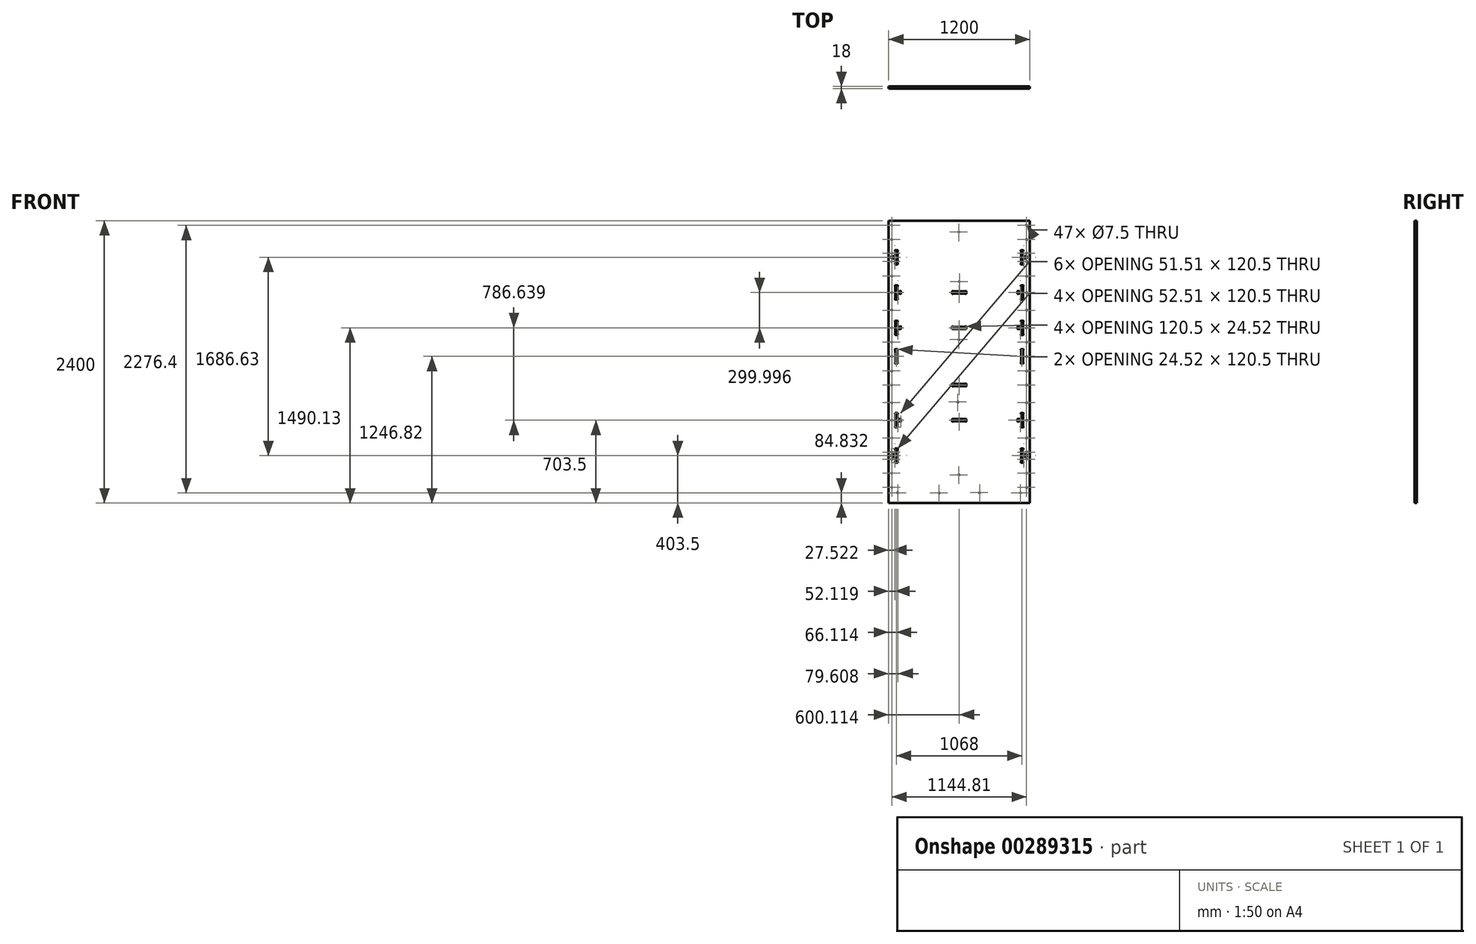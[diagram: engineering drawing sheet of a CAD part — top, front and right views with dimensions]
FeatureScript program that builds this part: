
annotation { "Feature Type Name" : "Feature", "Feature Type Description" : "" }
export const myFeature = defineFeature(function(context is Context, id is Id, definition is map)
    precondition{}
    {
        {
            var Q0;
            Q0=qCreatedBy(makeId("Front.planeOp"),FACE);
            var sketch = newSketch(context, id + "F0", { "sketchPlane" : qUnion([Q0])});
            skLineSegment(sketch, "E0", {"start": v(-600, -1200) * mm, "end": v(600, -1200) * mm});
            skLineSegment(sketch, "E1", {"start": v(600, -1200) * mm, "end": v(600, 1200) * mm});
            skLineSegment(sketch, "E2", {"start": v(600, 1200) * mm, "end": v(-600, 1200) * mm});
            skLineSegment(sketch, "E3", {"start": v(-600, 1200) * mm, "end": v(-600, -1200) * mm});
            skLineSegment(sketch, "E4", {"start": v(-599.64, -1096.25) * mm, "end": v(-543.14, -1096.25) * mm});
            skLineSegment(sketch, "E5", {"start": v(-543.14, -1096.25) * mm, "end": v(-543.14, -1042.52) * mm});
            skLineSegment(sketch, "E6", {"start": v(-543.14, -1042.52) * mm, "end": v(-543.14, -1042.29) * mm});
            skLineSegment(sketch, "E7", {"start": v(-543.14, -1042.29) * mm, "end": v(-543.37, -1042.27) * mm});
            skArc(sketch, "E8", {"start": v(-543.37, -1042.27) * mm, "mid": v(-546.15, -1039.15) * mm, "end": v(-543.14, -1036.25) * mm});
            skLineSegment(sketch, "E9", {"start": v(-543.14, -1036.25) * mm, "end": v(-524.64, -1036.25) * mm});
            skArc(sketch, "E10", {"start": v(-524.64, -1036.25) * mm, "mid": v(-521.63, -1039.15) * mm, "end": v(-524.4, -1042.27) * mm});
            skLineSegment(sketch, "E11", {"start": v(-524.4, -1042.27) * mm, "end": v(-524.64, -1042.29) * mm});
            skLineSegment(sketch, "E12", {"start": v(-524.64, -1042.29) * mm, "end": v(-524.64, -1042.52) * mm});
            skLineSegment(sketch, "E13", {"start": v(-524.64, -1042.52) * mm, "end": v(-524.64, -1087.24) * mm});
            skLineSegment(sketch, "E14", {"start": v(-524.64, -1087.24) * mm, "end": v(-500.9, -1087.24) * mm});
            skLineSegment(sketch, "E15", {"start": v(-500.9, -1087.24) * mm, "end": v(-500.67, -1087.24) * mm});
            skLineSegment(sketch, "E16", {"start": v(-500.67, -1087.24) * mm, "end": v(-500.66, -1087) * mm});
            skArc(sketch, "E17", {"start": v(-500.66, -1087) * mm, "mid": v(-497.54, -1084.22) * mm, "end": v(-494.64, -1087.24) * mm});
            skLineSegment(sketch, "E18", {"start": v(-494.64, -1087.24) * mm, "end": v(-494.64, -1096.25) * mm});
            skLineSegment(sketch, "E19", {"start": v(-494.64, -1096.25) * mm, "end": v(-60.14, -1096.25) * mm});
            skLineSegment(sketch, "E20", {"start": v(-60.14, -1096.25) * mm, "end": v(-60.14, -1087.25) * mm});
            skArc(sketch, "E21", {"start": v(-60.14, -1087.25) * mm, "mid": v(-57.24, -1084.24) * mm, "end": v(-54.11, -1087.02) * mm});
            skLineSegment(sketch, "E22", {"start": v(-54.11, -1087.02) * mm, "end": v(-54.1, -1087.25) * mm});
            skLineSegment(sketch, "E23", {"start": v(-54.1, -1087.25) * mm, "end": v(-53.87, -1087.25) * mm});
            skLineSegment(sketch, "E24", {"start": v(-53.87, -1087.25) * mm, "end": v(54.1, -1087.25) * mm});
            skLineSegment(sketch, "E25", {"start": v(54.1, -1087.25) * mm, "end": v(54.33, -1087.25) * mm});
            skLineSegment(sketch, "E26", {"start": v(54.33, -1087.25) * mm, "end": v(54.34, -1087.02) * mm});
            skArc(sketch, "E27", {"start": v(54.34, -1087.02) * mm, "mid": v(57.47, -1084.23) * mm, "end": v(60.36, -1087.25) * mm});
            skLineSegment(sketch, "E28", {"start": v(60.36, -1087.25) * mm, "end": v(60.36, -1096.26) * mm});
            skLineSegment(sketch, "E29", {"start": v(60.36, -1096.26) * mm, "end": v(494.86, -1096.23) * mm});
            skLineSegment(sketch, "E30", {"start": v(494.86, -1096.23) * mm, "end": v(494.86, -1087.26) * mm});
            skArc(sketch, "E31", {"start": v(494.86, -1087.26) * mm, "mid": v(497.76, -1084.25) * mm, "end": v(500.89, -1087.03) * mm});
            skLineSegment(sketch, "E32", {"start": v(500.89, -1087.03) * mm, "end": v(500.9, -1087.26) * mm});
            skLineSegment(sketch, "E33", {"start": v(500.9, -1087.26) * mm, "end": v(501.13, -1087.26) * mm});
            skLineSegment(sketch, "E34", {"start": v(501.13, -1087.26) * mm, "end": v(524.86, -1087.26) * mm});
            skLineSegment(sketch, "E35", {"start": v(524.86, -1087.26) * mm, "end": v(524.86, -1042.54) * mm});
            skLineSegment(sketch, "E36", {"start": v(524.86, -1042.54) * mm, "end": v(524.86, -1042.3) * mm});
            skLineSegment(sketch, "E37", {"start": v(524.86, -1042.3) * mm, "end": v(524.63, -1042.29) * mm});
            skArc(sketch, "E38", {"start": v(524.63, -1042.29) * mm, "mid": v(521.85, -1039.16) * mm, "end": v(524.86, -1036.27) * mm});
            skLineSegment(sketch, "E39", {"start": v(524.86, -1036.27) * mm, "end": v(543.36, -1036.27) * mm});
            skArc(sketch, "E40", {"start": v(543.36, -1036.27) * mm, "mid": v(546.37, -1039.17) * mm, "end": v(543.6, -1042.29) * mm});
            skLineSegment(sketch, "E41", {"start": v(543.6, -1042.29) * mm, "end": v(543.36, -1042.3) * mm});
            skLineSegment(sketch, "E42", {"start": v(543.36, -1042.3) * mm, "end": v(543.36, -1042.54) * mm});
            skLineSegment(sketch, "E43", {"start": v(543.36, -1042.54) * mm, "end": v(543.36, -1096.26) * mm});
            skLineSegment(sketch, "E44", {"start": v(543.36, -1096.26) * mm, "end": v(599.86, -1096.26) * mm});
            skLineSegment(sketch, "E45", {"start": v(599.86, -1096.26) * mm, "end": v(599.86, 1189.86) * mm});
            skLineSegment(sketch, "E46", {"start": v(599.86, 1189.86) * mm, "end": v(543.36, 1189.86) * mm});
            skLineSegment(sketch, "E47", {"start": v(543.36, 1189.86) * mm, "end": v(543.36, 1136.14) * mm});
            skLineSegment(sketch, "E48", {"start": v(543.36, 1136.14) * mm, "end": v(543.36, 1135.91) * mm});
            skLineSegment(sketch, "E49", {"start": v(543.36, 1135.91) * mm, "end": v(543.6, 1135.9) * mm});
            skArc(sketch, "E50", {"start": v(543.6, 1135.9) * mm, "mid": v(546.38, 1132.77) * mm, "end": v(543.36, 1129.87) * mm});
            skLineSegment(sketch, "E51", {"start": v(543.36, 1129.87) * mm, "end": v(524.86, 1129.87) * mm});
            skArc(sketch, "E52", {"start": v(524.86, 1129.87) * mm, "mid": v(521.85, 1132.77) * mm, "end": v(524.63, 1135.9) * mm});
            skLineSegment(sketch, "E53", {"start": v(524.63, 1135.9) * mm, "end": v(524.86, 1135.91) * mm});
            skLineSegment(sketch, "E54", {"start": v(524.86, 1135.91) * mm, "end": v(524.86, 1136.14) * mm});
            skLineSegment(sketch, "E55", {"start": v(524.86, 1136.14) * mm, "end": v(524.86, 1180.87) * mm});
            skLineSegment(sketch, "E56", {"start": v(524.86, 1180.87) * mm, "end": v(501.13, 1180.87) * mm});
            skLineSegment(sketch, "E57", {"start": v(501.13, 1180.87) * mm, "end": v(500.9, 1180.87) * mm});
            skLineSegment(sketch, "E58", {"start": v(500.9, 1180.87) * mm, "end": v(500.89, 1180.64) * mm});
            skArc(sketch, "E59", {"start": v(500.89, 1180.64) * mm, "mid": v(497.76, 1177.85) * mm, "end": v(494.86, 1180.87) * mm});
            skLineSegment(sketch, "E60", {"start": v(494.86, 1180.87) * mm, "end": v(494.86, 1189.87) * mm});
            skLineSegment(sketch, "E61", {"start": v(494.86, 1189.87) * mm, "end": v(60.36, 1189.87) * mm});
            skLineSegment(sketch, "E62", {"start": v(60.36, 1189.87) * mm, "end": v(60.36, 1180.87) * mm});
            skArc(sketch, "E63", {"start": v(60.36, 1180.87) * mm, "mid": v(57.46, 1177.86) * mm, "end": v(54.34, 1180.64) * mm});
            skLineSegment(sketch, "E64", {"start": v(54.34, 1180.64) * mm, "end": v(54.33, 1180.87) * mm});
            skLineSegment(sketch, "E65", {"start": v(54.33, 1180.87) * mm, "end": v(54.1, 1180.87) * mm});
            skLineSegment(sketch, "E66", {"start": v(54.1, 1180.87) * mm, "end": v(-53.87, 1180.87) * mm});
            skLineSegment(sketch, "E67", {"start": v(-53.87, 1180.87) * mm, "end": v(-54.1, 1180.87) * mm});
            skLineSegment(sketch, "E68", {"start": v(-54.1, 1180.87) * mm, "end": v(-54.12, 1180.64) * mm});
            skArc(sketch, "E69", {"start": v(-54.12, 1180.64) * mm, "mid": v(-57.24, 1177.85) * mm, "end": v(-60.14, 1180.87) * mm});
            skLineSegment(sketch, "E70", {"start": v(-60.14, 1180.87) * mm, "end": v(-60.14, 1189.87) * mm});
            skLineSegment(sketch, "E71", {"start": v(-60.14, 1189.87) * mm, "end": v(-494.64, 1189.88) * mm});
            skLineSegment(sketch, "E72", {"start": v(-494.64, 1189.88) * mm, "end": v(-494.64, 1180.87) * mm});
            skArc(sketch, "E73", {"start": v(-494.64, 1180.87) * mm, "mid": v(-497.54, 1177.86) * mm, "end": v(-500.66, 1180.64) * mm});
            skLineSegment(sketch, "E74", {"start": v(-500.66, 1180.64) * mm, "end": v(-500.68, 1180.87) * mm});
            skLineSegment(sketch, "E75", {"start": v(-500.68, 1180.87) * mm, "end": v(-500.9, 1180.87) * mm});
            skLineSegment(sketch, "E76", {"start": v(-500.9, 1180.87) * mm, "end": v(-524.64, 1180.87) * mm});
            skLineSegment(sketch, "E77", {"start": v(-524.64, 1180.87) * mm, "end": v(-524.64, 1136.15) * mm});
            skLineSegment(sketch, "E78", {"start": v(-524.64, 1136.15) * mm, "end": v(-524.64, 1135.92) * mm});
            skLineSegment(sketch, "E79", {"start": v(-524.64, 1135.92) * mm, "end": v(-524.4, 1135.9) * mm});
            skArc(sketch, "E80", {"start": v(-524.4, 1135.9) * mm, "mid": v(-521.62, 1132.78) * mm, "end": v(-524.64, 1129.88) * mm});
            skLineSegment(sketch, "E81", {"start": v(-524.64, 1129.88) * mm, "end": v(-543.14, 1129.88) * mm});
            skArc(sketch, "E82", {"start": v(-543.14, 1129.88) * mm, "mid": v(-546.15, 1132.78) * mm, "end": v(-543.37, 1135.9) * mm});
            skLineSegment(sketch, "E83", {"start": v(-543.37, 1135.9) * mm, "end": v(-543.14, 1135.92) * mm});
            skLineSegment(sketch, "E84", {"start": v(-543.14, 1135.92) * mm, "end": v(-543.14, 1136.15) * mm});
            skLineSegment(sketch, "E85", {"start": v(-543.14, 1136.15) * mm, "end": v(-543.14, 1189.88) * mm});
            skLineSegment(sketch, "E86", {"start": v(-543.14, 1189.88) * mm, "end": v(-599.64, 1189.88) * mm});
            skLineSegment(sketch, "E87", {"start": v(-543.14, 829.88) * mm, "end": v(-524.64, 829.88) * mm});
            skArc(sketch, "E88", {"start": v(-524.64, 829.88) * mm, "mid": v(-521.63, 832.9) * mm, "end": v(-524.64, 835.9) * mm});
            skLineSegment(sketch, "E89", {"start": v(-524.64, 835.9) * mm, "end": v(-524.63, 944.36) * mm});
            skArc(sketch, "E90", {"start": v(-524.63, 944.36) * mm, "mid": v(-521.62, 947.37) * mm, "end": v(-524.63, 950.38) * mm});
            skLineSegment(sketch, "E91", {"start": v(-524.63, 950.38) * mm, "end": v(-543.13, 950.38) * mm});
            skArc(sketch, "E92", {"start": v(-543.13, 950.38) * mm, "mid": v(-546.14, 947.38) * mm, "end": v(-543.13, 944.36) * mm});
            skLineSegment(sketch, "E93", {"start": v(-543.13, 944.36) * mm, "end": v(-543.14, 899.38) * mm});
            skLineSegment(sketch, "E94", {"start": v(-543.14, 899.38) * mm, "end": v(-568.12, 899.38) * mm});
            skArc(sketch, "E95", {"start": v(-568.12, 899.38) * mm, "mid": v(-571.13, 902.4) * mm, "end": v(-574.14, 899.38) * mm});
            skLineSegment(sketch, "E96", {"start": v(-574.14, 899.38) * mm, "end": v(-574.14, 880.88) * mm});
            skArc(sketch, "E97", {"start": v(-574.14, 880.88) * mm, "mid": v(-571.13, 877.87) * mm, "end": v(-568.12, 880.88) * mm});
            skLineSegment(sketch, "E98", {"start": v(-568.12, 880.88) * mm, "end": v(-543.14, 880.88) * mm});
            skLineSegment(sketch, "E99", {"start": v(-543.14, 880.88) * mm, "end": v(-543.14, 835.9) * mm});
            skArc(sketch, "E100", {"start": v(-543.14, 835.9) * mm, "mid": v(-546.15, 832.9) * mm, "end": v(-543.14, 829.88) * mm});
            skLineSegment(sketch, "E101", {"start": v(-524.64, 599.37) * mm, "end": v(-524.64, 644.36) * mm});
            skArc(sketch, "E102", {"start": v(-524.64, 644.36) * mm, "mid": v(-521.63, 647.37) * mm, "end": v(-524.64, 650.38) * mm});
            skLineSegment(sketch, "E103", {"start": v(-524.64, 650.38) * mm, "end": v(-543.14, 650.38) * mm});
            skArc(sketch, "E104", {"start": v(-543.14, 650.38) * mm, "mid": v(-546.15, 647.37) * mm, "end": v(-543.14, 644.36) * mm});
            skLineSegment(sketch, "E105", {"start": v(-543.14, 644.36) * mm, "end": v(-543.14, 535.9) * mm});
            skArc(sketch, "E106", {"start": v(-543.14, 535.9) * mm, "mid": v(-546.15, 532.9) * mm, "end": v(-543.14, 529.88) * mm});
            skLineSegment(sketch, "E107", {"start": v(-543.14, 529.88) * mm, "end": v(-524.64, 529.88) * mm});
            skArc(sketch, "E108", {"start": v(-524.64, 529.88) * mm, "mid": v(-521.63, 532.9) * mm, "end": v(-524.64, 535.9) * mm});
            skLineSegment(sketch, "E109", {"start": v(-524.64, 535.9) * mm, "end": v(-524.64, 580.87) * mm});
            skLineSegment(sketch, "E110", {"start": v(-524.64, 580.87) * mm, "end": v(-500.66, 580.87) * mm});
            skArc(sketch, "E111", {"start": v(-500.66, 580.87) * mm, "mid": v(-497.65, 577.86) * mm, "end": v(-494.64, 580.87) * mm});
            skLineSegment(sketch, "E112", {"start": v(-494.64, 580.87) * mm, "end": v(-494.64, 599.37) * mm});
            skArc(sketch, "E113", {"start": v(-494.64, 599.37) * mm, "mid": v(-497.65, 602.38) * mm, "end": v(-500.66, 599.37) * mm});
            skLineSegment(sketch, "E114", {"start": v(-500.66, 599.37) * mm, "end": v(-524.64, 599.37) * mm});
            skLineSegment(sketch, "E115", {"start": v(-524.64, 299.38) * mm, "end": v(-524.64, 344.37) * mm});
            skArc(sketch, "E116", {"start": v(-524.64, 344.37) * mm, "mid": v(-521.63, 347.38) * mm, "end": v(-524.64, 350.39) * mm});
            skLineSegment(sketch, "E117", {"start": v(-524.64, 350.39) * mm, "end": v(-543.14, 350.39) * mm});
            skArc(sketch, "E118", {"start": v(-543.14, 350.39) * mm, "mid": v(-546.15, 347.38) * mm, "end": v(-543.14, 344.37) * mm});
            skLineSegment(sketch, "E119", {"start": v(-543.14, 344.37) * mm, "end": v(-543.14, 235.9) * mm});
            skArc(sketch, "E120", {"start": v(-543.14, 235.9) * mm, "mid": v(-546.15, 232.9) * mm, "end": v(-543.14, 229.89) * mm});
            skLineSegment(sketch, "E121", {"start": v(-543.14, 229.89) * mm, "end": v(-524.64, 229.89) * mm});
            skArc(sketch, "E122", {"start": v(-524.64, 229.89) * mm, "mid": v(-521.63, 232.9) * mm, "end": v(-524.64, 235.9) * mm});
            skLineSegment(sketch, "E123", {"start": v(-524.64, 235.9) * mm, "end": v(-524.64, 280.88) * mm});
            skLineSegment(sketch, "E124", {"start": v(-524.64, 280.88) * mm, "end": v(-500.66, 280.88) * mm});
            skArc(sketch, "E125", {"start": v(-500.66, 280.88) * mm, "mid": v(-497.65, 277.87) * mm, "end": v(-494.64, 280.88) * mm});
            skLineSegment(sketch, "E126", {"start": v(-494.64, 280.88) * mm, "end": v(-494.64, 299.38) * mm});
            skArc(sketch, "E127", {"start": v(-494.64, 299.38) * mm, "mid": v(-497.65, 302.39) * mm, "end": v(-500.66, 299.38) * mm});
            skLineSegment(sketch, "E128", {"start": v(-500.66, 299.38) * mm, "end": v(-524.64, 299.38) * mm});
            skLineSegment(sketch, "E129", {"start": v(-524.64, -7.41) * mm, "end": v(-524.64, 101.05) * mm});
            skArc(sketch, "E130", {"start": v(-524.64, 101.05) * mm, "mid": v(-521.63, 104.06) * mm, "end": v(-524.64, 107.07) * mm});
            skLineSegment(sketch, "E131", {"start": v(-524.64, 107.07) * mm, "end": v(-543.14, 107.07) * mm});
            skArc(sketch, "E132", {"start": v(-543.14, 107.07) * mm, "mid": v(-546.15, 104.06) * mm, "end": v(-543.14, 101.05) * mm});
            skLineSegment(sketch, "E133", {"start": v(-543.14, 101.05) * mm, "end": v(-543.14, -7.41) * mm});
            skArc(sketch, "E134", {"start": v(-543.14, -7.41) * mm, "mid": v(-546.15, -10.42) * mm, "end": v(-543.14, -13.43) * mm});
            skLineSegment(sketch, "E135", {"start": v(-543.14, -13.43) * mm, "end": v(-524.64, -13.43) * mm});
            skArc(sketch, "E136", {"start": v(-524.64, -13.43) * mm, "mid": v(-521.63, -10.42) * mm, "end": v(-524.64, -7.41) * mm});
            skLineSegment(sketch, "E137", {"start": v(-524.64, -205.76) * mm, "end": v(-500.66, -205.76) * mm});
            skArc(sketch, "E138", {"start": v(-500.66, -205.76) * mm, "mid": v(-497.65, -208.77) * mm, "end": v(-494.64, -205.76) * mm});
            skLineSegment(sketch, "E139", {"start": v(-494.64, -205.76) * mm, "end": v(-494.64, -187.26) * mm});
            skArc(sketch, "E140", {"start": v(-494.64, -187.26) * mm, "mid": v(-497.65, -184.25) * mm, "end": v(-500.66, -187.26) * mm});
            skLineSegment(sketch, "E141", {"start": v(-500.66, -187.26) * mm, "end": v(-524.64, -187.26) * mm});
            skLineSegment(sketch, "E142", {"start": v(-524.64, -187.26) * mm, "end": v(-524.64, -142.27) * mm});
            skArc(sketch, "E143", {"start": v(-524.64, -142.27) * mm, "mid": v(-521.63, -139.26) * mm, "end": v(-524.64, -136.25) * mm});
            skLineSegment(sketch, "E144", {"start": v(-524.64, -136.25) * mm, "end": v(-543.14, -136.25) * mm});
            skArc(sketch, "E145", {"start": v(-543.14, -136.25) * mm, "mid": v(-546.15, -139.26) * mm, "end": v(-543.14, -142.27) * mm});
            skLineSegment(sketch, "E146", {"start": v(-543.14, -142.27) * mm, "end": v(-543.14, -250.73) * mm});
            skArc(sketch, "E147", {"start": v(-543.14, -250.73) * mm, "mid": v(-546.15, -253.74) * mm, "end": v(-543.14, -256.75) * mm});
            skLineSegment(sketch, "E148", {"start": v(-543.14, -256.75) * mm, "end": v(-524.64, -256.75) * mm});
            skArc(sketch, "E149", {"start": v(-524.64, -256.75) * mm, "mid": v(-521.63, -253.74) * mm, "end": v(-524.64, -250.73) * mm});
            skLineSegment(sketch, "E150", {"start": v(-524.64, -250.73) * mm, "end": v(-524.64, -205.76) * mm});
            skLineSegment(sketch, "E151", {"start": v(-500.66, -487.26) * mm, "end": v(-524.64, -487.26) * mm});
            skLineSegment(sketch, "E152", {"start": v(-524.64, -487.26) * mm, "end": v(-524.64, -442.27) * mm});
            skArc(sketch, "E153", {"start": v(-524.64, -442.27) * mm, "mid": v(-521.63, -439.26) * mm, "end": v(-524.64, -436.25) * mm});
            skLineSegment(sketch, "E154", {"start": v(-524.64, -436.25) * mm, "end": v(-543.14, -436.25) * mm});
            skArc(sketch, "E155", {"start": v(-543.14, -436.25) * mm, "mid": v(-546.15, -439.26) * mm, "end": v(-543.14, -442.27) * mm});
            skLineSegment(sketch, "E156", {"start": v(-543.14, -442.27) * mm, "end": v(-543.14, -550.73) * mm});
            skArc(sketch, "E157", {"start": v(-543.14, -550.73) * mm, "mid": v(-546.15, -553.74) * mm, "end": v(-543.14, -556.75) * mm});
            skLineSegment(sketch, "E158", {"start": v(-543.14, -556.75) * mm, "end": v(-524.64, -556.75) * mm});
            skArc(sketch, "E159", {"start": v(-524.64, -556.75) * mm, "mid": v(-521.63, -553.74) * mm, "end": v(-524.64, -550.73) * mm});
            skLineSegment(sketch, "E160", {"start": v(-524.64, -550.73) * mm, "end": v(-524.64, -505.76) * mm});
            skLineSegment(sketch, "E161", {"start": v(-524.64, -505.76) * mm, "end": v(-500.66, -505.76) * mm});
            skArc(sketch, "E162", {"start": v(-500.66, -505.76) * mm, "mid": v(-497.65, -508.77) * mm, "end": v(-494.64, -505.76) * mm});
            skLineSegment(sketch, "E163", {"start": v(-494.64, -505.76) * mm, "end": v(-494.64, -487.26) * mm});
            skArc(sketch, "E164", {"start": v(-494.64, -487.26) * mm, "mid": v(-497.65, -484.25) * mm, "end": v(-500.66, -487.26) * mm});
            skLineSegment(sketch, "E165", {"start": v(-524.64, -850.73) * mm, "end": v(-524.63, -742.27) * mm});
            skArc(sketch, "E166", {"start": v(-524.63, -742.27) * mm, "mid": v(-521.62, -739.26) * mm, "end": v(-524.63, -736.25) * mm});
            skLineSegment(sketch, "E167", {"start": v(-524.63, -736.25) * mm, "end": v(-543.13, -736.25) * mm});
            skArc(sketch, "E168", {"start": v(-543.13, -736.25) * mm, "mid": v(-546.14, -739.26) * mm, "end": v(-543.13, -742.27) * mm});
            skLineSegment(sketch, "E169", {"start": v(-543.13, -742.27) * mm, "end": v(-543.14, -787.25) * mm});
            skLineSegment(sketch, "E170", {"start": v(-543.14, -787.25) * mm, "end": v(-568.12, -787.25) * mm});
            skArc(sketch, "E171", {"start": v(-568.12, -787.25) * mm, "mid": v(-571.13, -784.24) * mm, "end": v(-574.14, -787.25) * mm});
            skLineSegment(sketch, "E172", {"start": v(-574.14, -787.25) * mm, "end": v(-574.14, -805.75) * mm});
            skArc(sketch, "E173", {"start": v(-574.14, -805.75) * mm, "mid": v(-571.13, -808.76) * mm, "end": v(-568.12, -805.75) * mm});
            skLineSegment(sketch, "E174", {"start": v(-568.12, -805.75) * mm, "end": v(-543.14, -805.75) * mm});
            skLineSegment(sketch, "E175", {"start": v(-543.14, -805.75) * mm, "end": v(-543.14, -850.73) * mm});
            skArc(sketch, "E176", {"start": v(-543.14, -850.73) * mm, "mid": v(-546.15, -853.74) * mm, "end": v(-543.14, -856.75) * mm});
            skLineSegment(sketch, "E177", {"start": v(-543.14, -856.75) * mm, "end": v(-524.64, -856.75) * mm});
            skArc(sketch, "E178", {"start": v(-524.64, -856.75) * mm, "mid": v(-521.63, -853.74) * mm, "end": v(-524.64, -850.73) * mm});
            skLineSegment(sketch, "E179", {"start": v(524.87, 944.35) * mm, "end": v(524.87, 835.9) * mm});
            skArc(sketch, "E180", {"start": v(524.87, 835.9) * mm, "mid": v(521.86, 832.88) * mm, "end": v(524.87, 829.87) * mm});
            skLineSegment(sketch, "E181", {"start": v(524.87, 829.87) * mm, "end": v(543.37, 829.87) * mm});
            skArc(sketch, "E182", {"start": v(543.37, 829.87) * mm, "mid": v(546.38, 832.88) * mm, "end": v(543.37, 835.9) * mm});
            skLineSegment(sketch, "E183", {"start": v(543.37, 835.9) * mm, "end": v(543.36, 880.87) * mm});
            skLineSegment(sketch, "E184", {"start": v(543.36, 880.87) * mm, "end": v(568.34, 880.87) * mm});
            skArc(sketch, "E185", {"start": v(568.34, 880.87) * mm, "mid": v(571.35, 877.86) * mm, "end": v(574.36, 880.87) * mm});
            skLineSegment(sketch, "E186", {"start": v(574.36, 880.87) * mm, "end": v(574.36, 899.37) * mm});
            skArc(sketch, "E187", {"start": v(574.36, 899.37) * mm, "mid": v(571.35, 902.38) * mm, "end": v(568.34, 899.37) * mm});
            skLineSegment(sketch, "E188", {"start": v(568.34, 899.37) * mm, "end": v(543.36, 899.37) * mm});
            skLineSegment(sketch, "E189", {"start": v(543.36, 899.37) * mm, "end": v(543.37, 944.35) * mm});
            skArc(sketch, "E190", {"start": v(543.37, 944.35) * mm, "mid": v(546.38, 947.36) * mm, "end": v(543.37, 950.37) * mm});
            skLineSegment(sketch, "E191", {"start": v(543.37, 950.37) * mm, "end": v(524.87, 950.37) * mm});
            skArc(sketch, "E192", {"start": v(524.87, 950.37) * mm, "mid": v(521.86, 947.36) * mm, "end": v(524.87, 944.35) * mm});
            skLineSegment(sketch, "E193", {"start": v(54.34, 599.37) * mm, "end": v(-54.12, 599.37) * mm});
            skArc(sketch, "E194", {"start": v(-54.12, 599.37) * mm, "mid": v(-57.13, 602.38) * mm, "end": v(-60.14, 599.37) * mm});
            skLineSegment(sketch, "E195", {"start": v(-60.14, 599.37) * mm, "end": v(-60.14, 580.87) * mm});
            skArc(sketch, "E196", {"start": v(-60.14, 580.87) * mm, "mid": v(-57.13, 577.86) * mm, "end": v(-54.12, 580.87) * mm});
            skLineSegment(sketch, "E197", {"start": v(-54.12, 580.87) * mm, "end": v(54.34, 580.87) * mm});
            skArc(sketch, "E198", {"start": v(54.34, 580.87) * mm, "mid": v(57.35, 577.86) * mm, "end": v(60.36, 580.87) * mm});
            skLineSegment(sketch, "E199", {"start": v(60.36, 580.87) * mm, "end": v(60.36, 599.37) * mm});
            skArc(sketch, "E200", {"start": v(60.36, 599.37) * mm, "mid": v(57.35, 602.38) * mm, "end": v(54.34, 599.37) * mm});
            skLineSegment(sketch, "E201", {"start": v(-54.12, 280.88) * mm, "end": v(54.34, 280.88) * mm});
            skArc(sketch, "E202", {"start": v(54.34, 280.88) * mm, "mid": v(57.35, 277.87) * mm, "end": v(60.36, 280.88) * mm});
            skLineSegment(sketch, "E203", {"start": v(60.36, 280.88) * mm, "end": v(60.36, 299.38) * mm});
            skArc(sketch, "E204", {"start": v(60.36, 299.38) * mm, "mid": v(57.35, 302.39) * mm, "end": v(54.34, 299.38) * mm});
            skLineSegment(sketch, "E205", {"start": v(54.34, 299.38) * mm, "end": v(-54.12, 299.38) * mm});
            skArc(sketch, "E206", {"start": v(-54.12, 299.38) * mm, "mid": v(-57.13, 302.39) * mm, "end": v(-60.14, 299.38) * mm});
            skLineSegment(sketch, "E207", {"start": v(-60.14, 299.38) * mm, "end": v(-60.14, 280.88) * mm});
            skArc(sketch, "E208", {"start": v(-60.14, 280.88) * mm, "mid": v(-57.13, 277.87) * mm, "end": v(-54.12, 280.88) * mm});
            skLineSegment(sketch, "E209", {"start": v(-54.12, -205.76) * mm, "end": v(54.34, -205.76) * mm});
            skArc(sketch, "E210", {"start": v(54.34, -205.76) * mm, "mid": v(57.35, -208.77) * mm, "end": v(60.36, -205.76) * mm});
            skLineSegment(sketch, "E211", {"start": v(60.36, -205.76) * mm, "end": v(60.36, -187.26) * mm});
            skArc(sketch, "E212", {"start": v(60.36, -187.26) * mm, "mid": v(57.35, -184.25) * mm, "end": v(54.34, -187.26) * mm});
            skLineSegment(sketch, "E213", {"start": v(54.34, -187.26) * mm, "end": v(-54.12, -187.26) * mm});
            skArc(sketch, "E214", {"start": v(-54.12, -187.26) * mm, "mid": v(-57.13, -184.25) * mm, "end": v(-60.14, -187.26) * mm});
            skLineSegment(sketch, "E215", {"start": v(-60.14, -187.26) * mm, "end": v(-60.14, -205.76) * mm});
            skArc(sketch, "E216", {"start": v(-60.14, -205.76) * mm, "mid": v(-57.13, -208.77) * mm, "end": v(-54.12, -205.76) * mm});
            skLineSegment(sketch, "E217", {"start": v(-54.12, -505.76) * mm, "end": v(54.34, -505.76) * mm});
            skArc(sketch, "E218", {"start": v(54.34, -505.76) * mm, "mid": v(57.35, -508.77) * mm, "end": v(60.36, -505.76) * mm});
            skLineSegment(sketch, "E219", {"start": v(60.36, -505.76) * mm, "end": v(60.36, -487.26) * mm});
            skArc(sketch, "E220", {"start": v(60.36, -487.26) * mm, "mid": v(57.35, -484.25) * mm, "end": v(54.34, -487.26) * mm});
            skLineSegment(sketch, "E221", {"start": v(54.34, -487.26) * mm, "end": v(-54.12, -487.26) * mm});
            skArc(sketch, "E222", {"start": v(-54.12, -487.26) * mm, "mid": v(-57.13, -484.25) * mm, "end": v(-60.14, -487.26) * mm});
            skLineSegment(sketch, "E223", {"start": v(-60.14, -487.26) * mm, "end": v(-60.14, -505.76) * mm});
            skArc(sketch, "E224", {"start": v(-60.14, -505.76) * mm, "mid": v(-57.13, -508.77) * mm, "end": v(-54.12, -505.76) * mm});
            skLineSegment(sketch, "E225", {"start": v(524.87, -742.28) * mm, "end": v(524.87, -850.74) * mm});
            skArc(sketch, "E226", {"start": v(524.87, -850.74) * mm, "mid": v(521.86, -853.75) * mm, "end": v(524.87, -856.76) * mm});
            skLineSegment(sketch, "E227", {"start": v(524.87, -856.76) * mm, "end": v(543.37, -856.76) * mm});
            skArc(sketch, "E228", {"start": v(543.37, -856.76) * mm, "mid": v(546.38, -853.75) * mm, "end": v(543.37, -850.74) * mm});
            skLineSegment(sketch, "E229", {"start": v(543.37, -850.74) * mm, "end": v(543.36, -805.77) * mm});
            skLineSegment(sketch, "E230", {"start": v(543.36, -805.77) * mm, "end": v(568.34, -805.77) * mm});
            skArc(sketch, "E231", {"start": v(568.34, -805.77) * mm, "mid": v(571.35, -808.78) * mm, "end": v(574.36, -805.77) * mm});
            skLineSegment(sketch, "E232", {"start": v(574.36, -805.77) * mm, "end": v(574.36, -787.27) * mm});
            skArc(sketch, "E233", {"start": v(574.36, -787.27) * mm, "mid": v(571.35, -784.26) * mm, "end": v(568.34, -787.27) * mm});
            skLineSegment(sketch, "E234", {"start": v(568.34, -787.27) * mm, "end": v(543.36, -787.27) * mm});
            skLineSegment(sketch, "E235", {"start": v(543.36, -787.27) * mm, "end": v(543.37, -742.28) * mm});
            skArc(sketch, "E236", {"start": v(543.37, -742.28) * mm, "mid": v(546.38, -739.27) * mm, "end": v(543.37, -736.26) * mm});
            skLineSegment(sketch, "E237", {"start": v(543.37, -736.26) * mm, "end": v(524.87, -736.26) * mm});
            skArc(sketch, "E238", {"start": v(524.87, -736.26) * mm, "mid": v(521.86, -739.27) * mm, "end": v(524.87, -742.28) * mm});
            skLineSegment(sketch, "E239", {"start": v(524.86, 599.37) * mm, "end": v(500.88, 599.37) * mm});
            skArc(sketch, "E240", {"start": v(500.88, 599.37) * mm, "mid": v(497.87, 602.38) * mm, "end": v(494.86, 599.37) * mm});
            skLineSegment(sketch, "E241", {"start": v(494.86, 599.37) * mm, "end": v(494.86, 580.87) * mm});
            skArc(sketch, "E242", {"start": v(494.86, 580.87) * mm, "mid": v(497.87, 577.86) * mm, "end": v(500.88, 580.87) * mm});
            skLineSegment(sketch, "E243", {"start": v(500.88, 580.87) * mm, "end": v(524.86, 580.87) * mm});
            skLineSegment(sketch, "E244", {"start": v(524.86, 580.87) * mm, "end": v(524.86, 535.9) * mm});
            skArc(sketch, "E245", {"start": v(524.86, 535.9) * mm, "mid": v(521.85, 532.89) * mm, "end": v(524.86, 529.88) * mm});
            skLineSegment(sketch, "E246", {"start": v(524.86, 529.88) * mm, "end": v(543.36, 529.88) * mm});
            skArc(sketch, "E247", {"start": v(543.36, 529.88) * mm, "mid": v(546.37, 532.89) * mm, "end": v(543.36, 535.9) * mm});
            skLineSegment(sketch, "E248", {"start": v(543.36, 535.9) * mm, "end": v(543.36, 644.36) * mm});
            skArc(sketch, "E249", {"start": v(543.36, 644.36) * mm, "mid": v(546.37, 647.37) * mm, "end": v(543.36, 650.38) * mm});
            skLineSegment(sketch, "E250", {"start": v(543.36, 650.38) * mm, "end": v(524.86, 650.38) * mm});
            skArc(sketch, "E251", {"start": v(524.86, 650.38) * mm, "mid": v(521.85, 647.37) * mm, "end": v(524.86, 644.36) * mm});
            skLineSegment(sketch, "E252", {"start": v(524.86, 644.36) * mm, "end": v(524.86, 599.37) * mm});
            skLineSegment(sketch, "E253", {"start": v(524.86, 299.38) * mm, "end": v(500.88, 299.38) * mm});
            skArc(sketch, "E254", {"start": v(500.88, 299.38) * mm, "mid": v(497.87, 302.39) * mm, "end": v(494.86, 299.38) * mm});
            skLineSegment(sketch, "E255", {"start": v(494.86, 299.38) * mm, "end": v(494.86, 280.88) * mm});
            skArc(sketch, "E256", {"start": v(494.86, 280.88) * mm, "mid": v(497.87, 277.87) * mm, "end": v(500.88, 280.88) * mm});
            skLineSegment(sketch, "E257", {"start": v(500.88, 280.88) * mm, "end": v(524.86, 280.88) * mm});
            skLineSegment(sketch, "E258", {"start": v(524.86, 280.88) * mm, "end": v(524.86, 235.9) * mm});
            skArc(sketch, "E259", {"start": v(524.86, 235.9) * mm, "mid": v(521.85, 232.9) * mm, "end": v(524.86, 229.88) * mm});
            skLineSegment(sketch, "E260", {"start": v(524.86, 229.88) * mm, "end": v(543.36, 229.88) * mm});
            skArc(sketch, "E261", {"start": v(543.36, 229.88) * mm, "mid": v(546.37, 232.9) * mm, "end": v(543.36, 235.9) * mm});
            skLineSegment(sketch, "E262", {"start": v(543.36, 235.9) * mm, "end": v(543.36, 344.36) * mm});
            skArc(sketch, "E263", {"start": v(543.36, 344.36) * mm, "mid": v(546.37, 347.37) * mm, "end": v(543.36, 350.38) * mm});
            skLineSegment(sketch, "E264", {"start": v(543.36, 350.38) * mm, "end": v(524.86, 350.38) * mm});
            skArc(sketch, "E265", {"start": v(524.86, 350.38) * mm, "mid": v(521.85, 347.37) * mm, "end": v(524.86, 344.36) * mm});
            skLineSegment(sketch, "E266", {"start": v(524.86, 344.36) * mm, "end": v(524.86, 299.38) * mm});
            skLineSegment(sketch, "E267", {"start": v(524.87, 101.03) * mm, "end": v(524.86, -7.43) * mm});
            skArc(sketch, "E268", {"start": v(524.86, -7.43) * mm, "mid": v(521.85, -10.44) * mm, "end": v(524.86, -13.45) * mm});
            skLineSegment(sketch, "E269", {"start": v(524.86, -13.45) * mm, "end": v(543.36, -13.45) * mm});
            skArc(sketch, "E270", {"start": v(543.36, -13.45) * mm, "mid": v(546.37, -10.44) * mm, "end": v(543.36, -7.43) * mm});
            skLineSegment(sketch, "E271", {"start": v(543.36, -7.43) * mm, "end": v(543.37, 101.03) * mm});
            skArc(sketch, "E272", {"start": v(543.37, 101.03) * mm, "mid": v(546.38, 104.04) * mm, "end": v(543.37, 107.05) * mm});
            skLineSegment(sketch, "E273", {"start": v(543.37, 107.05) * mm, "end": v(524.87, 107.05) * mm});
            skArc(sketch, "E274", {"start": v(524.87, 107.05) * mm, "mid": v(521.86, 104.04) * mm, "end": v(524.87, 101.03) * mm});
            skLineSegment(sketch, "E275", {"start": v(524.86, -187.26) * mm, "end": v(500.88, -187.26) * mm});
            skArc(sketch, "E276", {"start": v(500.88, -187.26) * mm, "mid": v(497.87, -184.25) * mm, "end": v(494.86, -187.26) * mm});
            skLineSegment(sketch, "E277", {"start": v(494.86, -187.26) * mm, "end": v(494.86, -205.76) * mm});
            skArc(sketch, "E278", {"start": v(494.86, -205.76) * mm, "mid": v(497.87, -208.77) * mm, "end": v(500.88, -205.76) * mm});
            skLineSegment(sketch, "E279", {"start": v(500.88, -205.76) * mm, "end": v(524.86, -205.76) * mm});
            skLineSegment(sketch, "E280", {"start": v(524.86, -205.76) * mm, "end": v(524.86, -250.74) * mm});
            skArc(sketch, "E281", {"start": v(524.86, -250.74) * mm, "mid": v(521.85, -253.75) * mm, "end": v(524.86, -256.76) * mm});
            skLineSegment(sketch, "E282", {"start": v(524.86, -256.76) * mm, "end": v(543.36, -256.76) * mm});
            skArc(sketch, "E283", {"start": v(543.36, -256.76) * mm, "mid": v(546.37, -253.75) * mm, "end": v(543.36, -250.74) * mm});
            skLineSegment(sketch, "E284", {"start": v(543.36, -250.74) * mm, "end": v(543.36, -142.28) * mm});
            skArc(sketch, "E285", {"start": v(543.36, -142.28) * mm, "mid": v(546.37, -139.27) * mm, "end": v(543.36, -136.26) * mm});
            skLineSegment(sketch, "E286", {"start": v(543.36, -136.26) * mm, "end": v(524.86, -136.26) * mm});
            skArc(sketch, "E287", {"start": v(524.86, -136.26) * mm, "mid": v(521.85, -139.27) * mm, "end": v(524.86, -142.28) * mm});
            skLineSegment(sketch, "E288", {"start": v(524.86, -142.28) * mm, "end": v(524.86, -187.26) * mm});
            skLineSegment(sketch, "E289", {"start": v(524.86, -487.26) * mm, "end": v(500.88, -487.26) * mm});
            skArc(sketch, "E290", {"start": v(500.88, -487.26) * mm, "mid": v(497.87, -484.25) * mm, "end": v(494.86, -487.26) * mm});
            skLineSegment(sketch, "E291", {"start": v(494.86, -487.26) * mm, "end": v(494.86, -505.76) * mm});
            skArc(sketch, "E292", {"start": v(494.86, -505.76) * mm, "mid": v(497.87, -508.77) * mm, "end": v(500.88, -505.76) * mm});
            skLineSegment(sketch, "E293", {"start": v(500.88, -505.76) * mm, "end": v(524.86, -505.76) * mm});
            skLineSegment(sketch, "E294", {"start": v(524.86, -505.76) * mm, "end": v(524.86, -550.74) * mm});
            skArc(sketch, "E295", {"start": v(524.86, -550.74) * mm, "mid": v(521.85, -553.75) * mm, "end": v(524.86, -556.76) * mm});
            skLineSegment(sketch, "E296", {"start": v(524.86, -556.76) * mm, "end": v(543.36, -556.76) * mm});
            skArc(sketch, "E297", {"start": v(543.36, -556.76) * mm, "mid": v(546.37, -553.75) * mm, "end": v(543.36, -550.74) * mm});
            skLineSegment(sketch, "E298", {"start": v(543.36, -550.74) * mm, "end": v(543.36, -442.28) * mm});
            skArc(sketch, "E299", {"start": v(543.36, -442.28) * mm, "mid": v(546.37, -439.27) * mm, "end": v(543.36, -436.26) * mm});
            skLineSegment(sketch, "E300", {"start": v(543.36, -436.26) * mm, "end": v(524.86, -436.26) * mm});
            skArc(sketch, "E301", {"start": v(524.86, -436.26) * mm, "mid": v(521.85, -439.27) * mm, "end": v(524.86, -442.28) * mm});
            skLineSegment(sketch, "E302", {"start": v(524.86, -442.28) * mm, "end": v(524.86, -487.26) * mm});
            skLineSegment(sketch, "E303", {"start": v(-92.84, 21.77) * mm, "end": v(-92.84, 61.76) * mm});
            skLineSegment(sketch, "E304", {"start": v(-92.84, 61.76) * mm, "end": v(-67.98, 61.76) * mm});
            skLineSegment(sketch, "E305", {"start": v(-92.84, 42.65) * mm, "end": v(-69.77, 42.65) * mm});
            skLineSegment(sketch, "E306", {"start": v(-35.68, 21.8) * mm, "end": v(-59.18, 21.8) * mm});
            skLineSegment(sketch, "E307", {"start": v(-59.18, 21.8) * mm, "end": v(-59.18, 61.74) * mm});
            skLineSegment(sketch, "E308", {"start": v(-20.52, 21.23) * mm, "end": v(-20.94, 21.23) * mm});
            skLineSegment(sketch, "E309", {"start": v(-20.94, 21.23) * mm, "end": v(-21.36, 21.24) * mm});
            skLineSegment(sketch, "E310", {"start": v(-21.36, 21.24) * mm, "end": v(-21.78, 21.25) * mm});
            skLineSegment(sketch, "E311", {"start": v(-21.78, 21.25) * mm, "end": v(-22.2, 21.28) * mm});
            skLineSegment(sketch, "E312", {"start": v(-22.2, 21.28) * mm, "end": v(-22.6, 21.32) * mm});
            skLineSegment(sketch, "E313", {"start": v(-22.6, 21.32) * mm, "end": v(-23.02, 21.37) * mm});
            skLineSegment(sketch, "E314", {"start": v(-23.02, 21.37) * mm, "end": v(-23.43, 21.43) * mm});
            skLineSegment(sketch, "E315", {"start": v(-23.43, 21.43) * mm, "end": v(-23.84, 21.5) * mm});
            skLineSegment(sketch, "E316", {"start": v(-23.84, 21.5) * mm, "end": v(-24.25, 21.58) * mm});
            skLineSegment(sketch, "E317", {"start": v(-24.25, 21.58) * mm, "end": v(-24.65, 21.67) * mm});
            skLineSegment(sketch, "E318", {"start": v(-24.65, 21.67) * mm, "end": v(-25.06, 21.77) * mm});
            skLineSegment(sketch, "E319", {"start": v(-25.06, 21.77) * mm, "end": v(-25.46, 21.88) * mm});
            skLineSegment(sketch, "E320", {"start": v(-25.46, 21.88) * mm, "end": v(-25.85, 22) * mm});
            skLineSegment(sketch, "E321", {"start": v(-25.85, 22) * mm, "end": v(-26.25, 22.12) * mm});
            skLineSegment(sketch, "E322", {"start": v(-26.25, 22.12) * mm, "end": v(-26.64, 22.26) * mm});
            skLineSegment(sketch, "E323", {"start": v(-26.64, 22.26) * mm, "end": v(-27.02, 22.41) * mm});
            skLineSegment(sketch, "E324", {"start": v(-27.02, 22.41) * mm, "end": v(-27.4, 22.57) * mm});
            skLineSegment(sketch, "E325", {"start": v(-27.4, 22.57) * mm, "end": v(-27.78, 22.74) * mm});
            skLineSegment(sketch, "E326", {"start": v(-27.78, 22.74) * mm, "end": v(-28.16, 22.91) * mm});
            skLineSegment(sketch, "E327", {"start": v(-28.16, 22.91) * mm, "end": v(-28.53, 23.1) * mm});
            skLineSegment(sketch, "E328", {"start": v(-28.53, 23.1) * mm, "end": v(-28.9, 23.3) * mm});
            skLineSegment(sketch, "E329", {"start": v(-28.9, 23.3) * mm, "end": v(-29.25, 23.5) * mm});
            skLineSegment(sketch, "E330", {"start": v(-29.25, 23.5) * mm, "end": v(-29.6, 23.71) * mm});
            skLineSegment(sketch, "E331", {"start": v(-29.6, 23.71) * mm, "end": v(-29.96, 23.93) * mm});
            skLineSegment(sketch, "E332", {"start": v(-29.96, 23.93) * mm, "end": v(-30.3, 24.17) * mm});
            skLineSegment(sketch, "E333", {"start": v(-30.3, 24.17) * mm, "end": v(-30.64, 24.4) * mm});
            skLineSegment(sketch, "E334", {"start": v(-30.64, 24.4) * mm, "end": v(-30.98, 24.65) * mm});
            skLineSegment(sketch, "E335", {"start": v(-30.98, 24.65) * mm, "end": v(-31.3, 24.91) * mm});
            skLineSegment(sketch, "E336", {"start": v(-31.3, 24.91) * mm, "end": v(-31.63, 25.18) * mm});
            skLineSegment(sketch, "E337", {"start": v(-31.63, 25.18) * mm, "end": v(-31.94, 25.45) * mm});
            skLineSegment(sketch, "E338", {"start": v(-31.94, 25.45) * mm, "end": v(-32.25, 25.73) * mm});
            skLineSegment(sketch, "E339", {"start": v(-32.25, 25.73) * mm, "end": v(-32.55, 26.03) * mm});
            skLineSegment(sketch, "E340", {"start": v(-32.55, 26.03) * mm, "end": v(-32.9, 26.4) * mm});
            skLineSegment(sketch, "E341", {"start": v(-32.9, 26.4) * mm, "end": v(-33.24, 26.8) * mm});
            skLineSegment(sketch, "E342", {"start": v(-33.24, 26.8) * mm, "end": v(-33.57, 27.2) * mm});
            skLineSegment(sketch, "E343", {"start": v(-33.57, 27.2) * mm, "end": v(-33.9, 27.6) * mm});
            skLineSegment(sketch, "E344", {"start": v(-33.9, 27.6) * mm, "end": v(-34.2, 28) * mm});
            skLineSegment(sketch, "E345", {"start": v(-34.2, 28) * mm, "end": v(-34.5, 28.42) * mm});
            skLineSegment(sketch, "E346", {"start": v(-34.5, 28.42) * mm, "end": v(-34.78, 28.85) * mm});
            skLineSegment(sketch, "E347", {"start": v(-34.78, 28.85) * mm, "end": v(-35.06, 29.28) * mm});
            skLineSegment(sketch, "E348", {"start": v(-35.06, 29.28) * mm, "end": v(-35.32, 29.71) * mm});
            skLineSegment(sketch, "E349", {"start": v(-35.32, 29.71) * mm, "end": v(-35.58, 30.16) * mm});
            skLineSegment(sketch, "E350", {"start": v(-35.58, 30.16) * mm, "end": v(-35.82, 30.6) * mm});
            skLineSegment(sketch, "E351", {"start": v(-35.82, 30.6) * mm, "end": v(-36.05, 31.06) * mm});
            skLineSegment(sketch, "E352", {"start": v(-36.05, 31.06) * mm, "end": v(-36.27, 31.52) * mm});
            skLineSegment(sketch, "E353", {"start": v(-36.27, 31.52) * mm, "end": v(-36.48, 31.98) * mm});
            skLineSegment(sketch, "E354", {"start": v(-36.48, 31.98) * mm, "end": v(-36.68, 32.45) * mm});
            skLineSegment(sketch, "E355", {"start": v(-36.68, 32.45) * mm, "end": v(-36.86, 32.93) * mm});
            skLineSegment(sketch, "E356", {"start": v(-36.86, 32.93) * mm, "end": v(-37.04, 33.4) * mm});
            skLineSegment(sketch, "E357", {"start": v(-37.04, 33.4) * mm, "end": v(-37.2, 33.89) * mm});
            skLineSegment(sketch, "E358", {"start": v(-37.2, 33.89) * mm, "end": v(-37.35, 34.38) * mm});
            skLineSegment(sketch, "E359", {"start": v(-37.35, 34.38) * mm, "end": v(-37.49, 34.87) * mm});
            skLineSegment(sketch, "E360", {"start": v(-37.49, 34.87) * mm, "end": v(-37.61, 35.36) * mm});
            skLineSegment(sketch, "E361", {"start": v(-37.61, 35.36) * mm, "end": v(-37.73, 35.86) * mm});
            skLineSegment(sketch, "E362", {"start": v(-37.73, 35.86) * mm, "end": v(-37.83, 36.36) * mm});
            skLineSegment(sketch, "E363", {"start": v(-37.83, 36.36) * mm, "end": v(-37.92, 36.86) * mm});
            skLineSegment(sketch, "E364", {"start": v(-37.92, 36.86) * mm, "end": v(-38, 37.37) * mm});
            skLineSegment(sketch, "E365", {"start": v(-38, 37.37) * mm, "end": v(-38.06, 37.87) * mm});
            skLineSegment(sketch, "E366", {"start": v(-38.06, 37.87) * mm, "end": v(-38.11, 38.38) * mm});
            skLineSegment(sketch, "E367", {"start": v(-38.11, 38.38) * mm, "end": v(-38.15, 38.9) * mm});
            skLineSegment(sketch, "E368", {"start": v(-38.15, 38.9) * mm, "end": v(-38.18, 39.4) * mm});
            skLineSegment(sketch, "E369", {"start": v(-38.18, 39.4) * mm, "end": v(-38.2, 39.92) * mm});
            skLineSegment(sketch, "E370", {"start": v(-38.2, 39.92) * mm, "end": v(-38.2, 40.44) * mm});
            skLineSegment(sketch, "E371", {"start": v(-38.2, 40.44) * mm, "end": v(-38.18, 40.96) * mm});
            skLineSegment(sketch, "E372", {"start": v(-38.18, 40.96) * mm, "end": v(-38.2, 41.52) * mm});
            skLineSegment(sketch, "E373", {"start": v(-38.2, 41.52) * mm, "end": v(-38.2, 42.08) * mm});
            skLineSegment(sketch, "E374", {"start": v(-38.2, 42.08) * mm, "end": v(-38.19, 42.64) * mm});
            skLineSegment(sketch, "E375", {"start": v(-38.19, 42.64) * mm, "end": v(-38.16, 43.2) * mm});
            skLineSegment(sketch, "E376", {"start": v(-38.16, 43.2) * mm, "end": v(-38.12, 43.75) * mm});
            skLineSegment(sketch, "E377", {"start": v(-38.12, 43.75) * mm, "end": v(-38.06, 44.3) * mm});
            skLineSegment(sketch, "E378", {"start": v(-38.06, 44.3) * mm, "end": v(-38, 44.86) * mm});
            skLineSegment(sketch, "E379", {"start": v(-38, 44.86) * mm, "end": v(-37.91, 45.4) * mm});
            skLineSegment(sketch, "E380", {"start": v(-37.91, 45.4) * mm, "end": v(-37.82, 45.95) * mm});
            skLineSegment(sketch, "E381", {"start": v(-37.82, 45.95) * mm, "end": v(-37.71, 46.5) * mm});
            skLineSegment(sketch, "E382", {"start": v(-37.71, 46.5) * mm, "end": v(-37.59, 47.03) * mm});
            skLineSegment(sketch, "E383", {"start": v(-37.59, 47.03) * mm, "end": v(-37.45, 47.57) * mm});
            skLineSegment(sketch, "E384", {"start": v(-37.45, 47.57) * mm, "end": v(-37.3, 48.1) * mm});
            skLineSegment(sketch, "E385", {"start": v(-37.3, 48.1) * mm, "end": v(-37.14, 48.63) * mm});
            skLineSegment(sketch, "E386", {"start": v(-37.14, 48.63) * mm, "end": v(-36.97, 49.16) * mm});
            skLineSegment(sketch, "E387", {"start": v(-36.97, 49.16) * mm, "end": v(-36.78, 49.68) * mm});
            skLineSegment(sketch, "E388", {"start": v(-36.78, 49.68) * mm, "end": v(-36.58, 50.2) * mm});
            skLineSegment(sketch, "E389", {"start": v(-36.58, 50.2) * mm, "end": v(-36.36, 50.7) * mm});
            skLineSegment(sketch, "E390", {"start": v(-36.36, 50.7) * mm, "end": v(-36.14, 51.2) * mm});
            skLineSegment(sketch, "E391", {"start": v(-36.14, 51.2) * mm, "end": v(-35.9, 51.7) * mm});
            skLineSegment(sketch, "E392", {"start": v(-35.9, 51.7) * mm, "end": v(-35.65, 52.2) * mm});
            skLineSegment(sketch, "E393", {"start": v(-35.65, 52.2) * mm, "end": v(-35.38, 52.69) * mm});
            skLineSegment(sketch, "E394", {"start": v(-35.38, 52.69) * mm, "end": v(-35.1, 53.17) * mm});
            skLineSegment(sketch, "E395", {"start": v(-35.1, 53.17) * mm, "end": v(-34.82, 53.64) * mm});
            skLineSegment(sketch, "E396", {"start": v(-34.82, 53.64) * mm, "end": v(-34.52, 54.1) * mm});
            skLineSegment(sketch, "E397", {"start": v(-34.52, 54.1) * mm, "end": v(-34.2, 54.57) * mm});
            skLineSegment(sketch, "E398", {"start": v(-34.2, 54.57) * mm, "end": v(-33.88, 55.02) * mm});
            skLineSegment(sketch, "E399", {"start": v(-33.88, 55.02) * mm, "end": v(-33.55, 55.47) * mm});
            skLineSegment(sketch, "E400", {"start": v(-33.55, 55.47) * mm, "end": v(-33.2, 55.9) * mm});
            skLineSegment(sketch, "E401", {"start": v(-33.2, 55.9) * mm, "end": v(-32.84, 56.33) * mm});
            skLineSegment(sketch, "E402", {"start": v(-32.84, 56.33) * mm, "end": v(-32.47, 56.75) * mm});
            skLineSegment(sketch, "E403", {"start": v(-32.47, 56.75) * mm, "end": v(-32.1, 57.16) * mm});
            skLineSegment(sketch, "E404", {"start": v(-32.1, 57.16) * mm, "end": v(-31.8, 57.46) * mm});
            skLineSegment(sketch, "E405", {"start": v(-31.8, 57.46) * mm, "end": v(-31.51, 57.74) * mm});
            skLineSegment(sketch, "E406", {"start": v(-31.51, 57.74) * mm, "end": v(-31.21, 58.01) * mm});
            skLineSegment(sketch, "E407", {"start": v(-31.21, 58.01) * mm, "end": v(-30.9, 58.28) * mm});
            skLineSegment(sketch, "E408", {"start": v(-30.9, 58.28) * mm, "end": v(-30.6, 58.54) * mm});
            skLineSegment(sketch, "E409", {"start": v(-30.6, 58.54) * mm, "end": v(-30.28, 58.78) * mm});
            skLineSegment(sketch, "E410", {"start": v(-30.28, 58.78) * mm, "end": v(-29.95, 59.02) * mm});
            skLineSegment(sketch, "E411", {"start": v(-29.95, 59.02) * mm, "end": v(-29.62, 59.26) * mm});
            skLineSegment(sketch, "E412", {"start": v(-29.62, 59.26) * mm, "end": v(-29.29, 59.48) * mm});
            skLineSegment(sketch, "E413", {"start": v(-29.29, 59.48) * mm, "end": v(-28.95, 59.7) * mm});
            skLineSegment(sketch, "E414", {"start": v(-28.95, 59.7) * mm, "end": v(-28.6, 59.9) * mm});
            skLineSegment(sketch, "E415", {"start": v(-28.6, 59.9) * mm, "end": v(-28.25, 60.1) * mm});
            skLineSegment(sketch, "E416", {"start": v(-28.25, 60.1) * mm, "end": v(-27.9, 60.28) * mm});
            skLineSegment(sketch, "E417", {"start": v(-27.9, 60.28) * mm, "end": v(-27.54, 60.46) * mm});
            skLineSegment(sketch, "E418", {"start": v(-27.54, 60.46) * mm, "end": v(-27.17, 60.63) * mm});
            skLineSegment(sketch, "E419", {"start": v(-27.17, 60.63) * mm, "end": v(-26.8, 60.78) * mm});
            skLineSegment(sketch, "E420", {"start": v(-26.8, 60.78) * mm, "end": v(-26.43, 60.93) * mm});
            skLineSegment(sketch, "E421", {"start": v(-26.43, 60.93) * mm, "end": v(-26.06, 61.07) * mm});
            skLineSegment(sketch, "E422", {"start": v(-26.06, 61.07) * mm, "end": v(-25.68, 61.2) * mm});
            skLineSegment(sketch, "E423", {"start": v(-25.68, 61.2) * mm, "end": v(-25.3, 61.33) * mm});
            skLineSegment(sketch, "E424", {"start": v(-25.3, 61.33) * mm, "end": v(-24.9, 61.44) * mm});
            skLineSegment(sketch, "E425", {"start": v(-24.9, 61.44) * mm, "end": v(-24.52, 61.54) * mm});
            skLineSegment(sketch, "E426", {"start": v(-24.52, 61.54) * mm, "end": v(-24.13, 61.63) * mm});
            skLineSegment(sketch, "E427", {"start": v(-24.13, 61.63) * mm, "end": v(-23.73, 61.71) * mm});
            skLineSegment(sketch, "E428", {"start": v(-23.73, 61.71) * mm, "end": v(-23.34, 61.78) * mm});
            skLineSegment(sketch, "E429", {"start": v(-23.34, 61.78) * mm, "end": v(-22.94, 61.84) * mm});
            skLineSegment(sketch, "E430", {"start": v(-22.94, 61.84) * mm, "end": v(-22.54, 61.9) * mm});
            skLineSegment(sketch, "E431", {"start": v(-22.54, 61.9) * mm, "end": v(-22.14, 61.93) * mm});
            skLineSegment(sketch, "E432", {"start": v(-22.14, 61.93) * mm, "end": v(-21.73, 61.96) * mm});
            skLineSegment(sketch, "E433", {"start": v(-21.73, 61.96) * mm, "end": v(-21.33, 61.98) * mm});
            skLineSegment(sketch, "E434", {"start": v(-21.33, 61.98) * mm, "end": v(-20.92, 62) * mm});
            skLineSegment(sketch, "E435", {"start": v(-20.92, 62) * mm, "end": v(-20.51, 62) * mm});
            skLineSegment(sketch, "E436", {"start": v(-20.51, 62) * mm, "end": v(-20.1, 61.99) * mm});
            skLineSegment(sketch, "E437", {"start": v(-20.1, 61.99) * mm, "end": v(-19.68, 61.97) * mm});
            skLineSegment(sketch, "E438", {"start": v(-19.68, 61.97) * mm, "end": v(-19.27, 61.95) * mm});
            skLineSegment(sketch, "E439", {"start": v(-19.27, 61.95) * mm, "end": v(-18.86, 61.91) * mm});
            skLineSegment(sketch, "E440", {"start": v(-18.86, 61.91) * mm, "end": v(-18.45, 61.87) * mm});
            skLineSegment(sketch, "E441", {"start": v(-18.45, 61.87) * mm, "end": v(-18.05, 61.8) * mm});
            skLineSegment(sketch, "E442", {"start": v(-18.05, 61.8) * mm, "end": v(-17.64, 61.74) * mm});
            skLineSegment(sketch, "E443", {"start": v(-17.64, 61.74) * mm, "end": v(-17.24, 61.66) * mm});
            skLineSegment(sketch, "E444", {"start": v(-17.24, 61.66) * mm, "end": v(-16.84, 61.58) * mm});
            skLineSegment(sketch, "E445", {"start": v(-16.84, 61.58) * mm, "end": v(-16.44, 61.48) * mm});
            skLineSegment(sketch, "E446", {"start": v(-16.44, 61.48) * mm, "end": v(-16.05, 61.37) * mm});
            skLineSegment(sketch, "E447", {"start": v(-16.05, 61.37) * mm, "end": v(-15.66, 61.25) * mm});
            skLineSegment(sketch, "E448", {"start": v(-15.66, 61.25) * mm, "end": v(-15.27, 61.13) * mm});
            skLineSegment(sketch, "E449", {"start": v(-15.27, 61.13) * mm, "end": v(-14.89, 60.99) * mm});
            skLineSegment(sketch, "E450", {"start": v(-14.89, 60.99) * mm, "end": v(-14.5, 60.84) * mm});
            skLineSegment(sketch, "E451", {"start": v(-14.5, 60.84) * mm, "end": v(-14.13, 60.68) * mm});
            skLineSegment(sketch, "E452", {"start": v(-14.13, 60.68) * mm, "end": v(-13.76, 60.52) * mm});
            skLineSegment(sketch, "E453", {"start": v(-13.76, 60.52) * mm, "end": v(-13.4, 60.34) * mm});
            skLineSegment(sketch, "E454", {"start": v(-13.4, 60.34) * mm, "end": v(-13.03, 60.16) * mm});
            skLineSegment(sketch, "E455", {"start": v(-13.03, 60.16) * mm, "end": v(-12.67, 59.96) * mm});
            skLineSegment(sketch, "E456", {"start": v(-12.67, 59.96) * mm, "end": v(-12.31, 59.76) * mm});
            skLineSegment(sketch, "E457", {"start": v(-12.31, 59.76) * mm, "end": v(-11.97, 59.55) * mm});
            skLineSegment(sketch, "E458", {"start": v(-11.97, 59.55) * mm, "end": v(-11.62, 59.33) * mm});
            skLineSegment(sketch, "E459", {"start": v(-11.62, 59.33) * mm, "end": v(-11.28, 59.1) * mm});
            skLineSegment(sketch, "E460", {"start": v(-11.28, 59.1) * mm, "end": v(-10.95, 58.86) * mm});
            skLineSegment(sketch, "E461", {"start": v(-10.95, 58.86) * mm, "end": v(-10.63, 58.6) * mm});
            skLineSegment(sketch, "E462", {"start": v(-10.63, 58.6) * mm, "end": v(-10.3, 58.35) * mm});
            skLineSegment(sketch, "E463", {"start": v(-10.3, 58.35) * mm, "end": v(-10, 58.09) * mm});
            skLineSegment(sketch, "E464", {"start": v(-10, 58.09) * mm, "end": v(-9.68, 57.81) * mm});
            skLineSegment(sketch, "E465", {"start": v(-9.68, 57.81) * mm, "end": v(-9.38, 57.53) * mm});
            skLineSegment(sketch, "E466", {"start": v(-9.38, 57.53) * mm, "end": v(-9.09, 57.24) * mm});
            skLineSegment(sketch, "E467", {"start": v(-9.09, 57.24) * mm, "end": v(-8.8, 56.94) * mm});
            skLineSegment(sketch, "E468", {"start": v(-8.8, 56.94) * mm, "end": v(-8.43, 56.53) * mm});
            skLineSegment(sketch, "E469", {"start": v(-8.43, 56.53) * mm, "end": v(-8.07, 56.11) * mm});
            skLineSegment(sketch, "E470", {"start": v(-8.07, 56.11) * mm, "end": v(-7.73, 55.69) * mm});
            skLineSegment(sketch, "E471", {"start": v(-7.73, 55.69) * mm, "end": v(-7.39, 55.25) * mm});
            skLineSegment(sketch, "E472", {"start": v(-7.39, 55.25) * mm, "end": v(-7.06, 54.81) * mm});
            skLineSegment(sketch, "E473", {"start": v(-7.06, 54.81) * mm, "end": v(-6.75, 54.36) * mm});
            skLineSegment(sketch, "E474", {"start": v(-6.75, 54.36) * mm, "end": v(-6.45, 53.9) * mm});
            skLineSegment(sketch, "E475", {"start": v(-6.45, 53.9) * mm, "end": v(-6.16, 53.44) * mm});
            skLineSegment(sketch, "E476", {"start": v(-6.16, 53.44) * mm, "end": v(-5.88, 52.97) * mm});
            skLineSegment(sketch, "E477", {"start": v(-5.88, 52.97) * mm, "end": v(-5.62, 52.5) * mm});
            skLineSegment(sketch, "E478", {"start": v(-5.62, 52.5) * mm, "end": v(-5.36, 52.02) * mm});
            skLineSegment(sketch, "E479", {"start": v(-5.36, 52.02) * mm, "end": v(-5.12, 51.53) * mm});
            skLineSegment(sketch, "E480", {"start": v(-5.12, 51.53) * mm, "end": v(-4.89, 51.04) * mm});
            skLineSegment(sketch, "E481", {"start": v(-4.89, 51.04) * mm, "end": v(-4.67, 50.54) * mm});
            skLineSegment(sketch, "E482", {"start": v(-4.67, 50.54) * mm, "end": v(-4.47, 50.03) * mm});
            skLineSegment(sketch, "E483", {"start": v(-4.47, 50.03) * mm, "end": v(-4.27, 49.52) * mm});
            skLineSegment(sketch, "E484", {"start": v(-4.27, 49.52) * mm, "end": v(-4.1, 49.01) * mm});
            skLineSegment(sketch, "E485", {"start": v(-4.1, 49.01) * mm, "end": v(-3.93, 48.5) * mm});
            skLineSegment(sketch, "E486", {"start": v(-3.93, 48.5) * mm, "end": v(-3.77, 47.97) * mm});
            skLineSegment(sketch, "E487", {"start": v(-3.77, 47.97) * mm, "end": v(-3.63, 47.45) * mm});
            skLineSegment(sketch, "E488", {"start": v(-3.63, 47.45) * mm, "end": v(-3.5, 46.92) * mm});
            skLineSegment(sketch, "E489", {"start": v(-3.5, 46.92) * mm, "end": v(-3.39, 46.38) * mm});
            skLineSegment(sketch, "E490", {"start": v(-3.39, 46.38) * mm, "end": v(-3.28, 45.85) * mm});
            skLineSegment(sketch, "E491", {"start": v(-3.28, 45.85) * mm, "end": v(-3.2, 45.3) * mm});
            skLineSegment(sketch, "E492", {"start": v(-3.2, 45.3) * mm, "end": v(-3.12, 44.77) * mm});
            skLineSegment(sketch, "E493", {"start": v(-3.12, 44.77) * mm, "end": v(-3.06, 44.23) * mm});
            skLineSegment(sketch, "E494", {"start": v(-3.06, 44.23) * mm, "end": v(-3, 43.68) * mm});
            skLineSegment(sketch, "E495", {"start": v(-3, 43.68) * mm, "end": v(-2.97, 43.13) * mm});
            skLineSegment(sketch, "E496", {"start": v(-2.97, 43.13) * mm, "end": v(-2.95, 42.59) * mm});
            skLineSegment(sketch, "E497", {"start": v(-2.95, 42.59) * mm, "end": v(-2.94, 42.04) * mm});
            skLineSegment(sketch, "E498", {"start": v(-2.94, 42.04) * mm, "end": v(-2.95, 41.48) * mm});
            skLineSegment(sketch, "E499", {"start": v(-2.95, 41.48) * mm, "end": v(-2.97, 40.93) * mm});
            skLineSegment(sketch, "E500", {"start": v(-2.97, 40.93) * mm, "end": v(-2.96, 40.42) * mm});
            skLineSegment(sketch, "E501", {"start": v(-2.96, 40.42) * mm, "end": v(-2.96, 39.9) * mm});
            skLineSegment(sketch, "E502", {"start": v(-2.96, 39.9) * mm, "end": v(-2.98, 39.4) * mm});
            skLineSegment(sketch, "E503", {"start": v(-2.98, 39.4) * mm, "end": v(-3.01, 38.88) * mm});
            skLineSegment(sketch, "E504", {"start": v(-3.01, 38.88) * mm, "end": v(-3.06, 38.37) * mm});
            skLineSegment(sketch, "E505", {"start": v(-3.06, 38.37) * mm, "end": v(-3.11, 37.86) * mm});
            skLineSegment(sketch, "E506", {"start": v(-3.11, 37.86) * mm, "end": v(-3.18, 37.36) * mm});
            skLineSegment(sketch, "E507", {"start": v(-3.18, 37.36) * mm, "end": v(-3.26, 36.86) * mm});
            skLineSegment(sketch, "E508", {"start": v(-3.26, 36.86) * mm, "end": v(-3.35, 36.36) * mm});
            skLineSegment(sketch, "E509", {"start": v(-3.35, 36.36) * mm, "end": v(-3.46, 35.86) * mm});
            skLineSegment(sketch, "E510", {"start": v(-3.46, 35.86) * mm, "end": v(-3.58, 35.36) * mm});
            skLineSegment(sketch, "E511", {"start": v(-3.58, 35.36) * mm, "end": v(-3.7, 34.87) * mm});
            skLineSegment(sketch, "E512", {"start": v(-3.7, 34.87) * mm, "end": v(-3.85, 34.39) * mm});
            skLineSegment(sketch, "E513", {"start": v(-3.85, 34.39) * mm, "end": v(-4, 33.9) * mm});
            skLineSegment(sketch, "E514", {"start": v(-4, 33.9) * mm, "end": v(-4.17, 33.42) * mm});
            skLineSegment(sketch, "E515", {"start": v(-4.17, 33.42) * mm, "end": v(-4.35, 32.95) * mm});
            skLineSegment(sketch, "E516", {"start": v(-4.35, 32.95) * mm, "end": v(-4.54, 32.48) * mm});
            skLineSegment(sketch, "E517", {"start": v(-4.54, 32.48) * mm, "end": v(-4.74, 32.01) * mm});
            skLineSegment(sketch, "E518", {"start": v(-4.74, 32.01) * mm, "end": v(-4.96, 31.55) * mm});
            skLineSegment(sketch, "E519", {"start": v(-4.96, 31.55) * mm, "end": v(-5.18, 31.1) * mm});
            skLineSegment(sketch, "E520", {"start": v(-5.18, 31.1) * mm, "end": v(-5.42, 30.65) * mm});
            skLineSegment(sketch, "E521", {"start": v(-5.42, 30.65) * mm, "end": v(-5.66, 30.2) * mm});
            skLineSegment(sketch, "E522", {"start": v(-5.66, 30.2) * mm, "end": v(-5.92, 29.76) * mm});
            skLineSegment(sketch, "E523", {"start": v(-5.92, 29.76) * mm, "end": v(-6.19, 29.33) * mm});
            skLineSegment(sketch, "E524", {"start": v(-6.19, 29.33) * mm, "end": v(-6.47, 28.9) * mm});
            skLineSegment(sketch, "E525", {"start": v(-6.47, 28.9) * mm, "end": v(-6.76, 28.49) * mm});
            skLineSegment(sketch, "E526", {"start": v(-6.76, 28.49) * mm, "end": v(-7.06, 28.08) * mm});
            skLineSegment(sketch, "E527", {"start": v(-7.06, 28.08) * mm, "end": v(-7.38, 27.67) * mm});
            skLineSegment(sketch, "E528", {"start": v(-7.38, 27.67) * mm, "end": v(-7.7, 27.27) * mm});
            skLineSegment(sketch, "E529", {"start": v(-7.7, 27.27) * mm, "end": v(-8.03, 26.89) * mm});
            skLineSegment(sketch, "E530", {"start": v(-8.03, 26.89) * mm, "end": v(-8.38, 26.5) * mm});
            skLineSegment(sketch, "E531", {"start": v(-8.38, 26.5) * mm, "end": v(-8.73, 26.13) * mm});
            skLineSegment(sketch, "E532", {"start": v(-8.73, 26.13) * mm, "end": v(-9.02, 25.84) * mm});
            skLineSegment(sketch, "E533", {"start": v(-9.02, 25.84) * mm, "end": v(-9.32, 25.56) * mm});
            skLineSegment(sketch, "E534", {"start": v(-9.32, 25.56) * mm, "end": v(-9.63, 25.28) * mm});
            skLineSegment(sketch, "E535", {"start": v(-9.63, 25.28) * mm, "end": v(-9.95, 25.01) * mm});
            skLineSegment(sketch, "E536", {"start": v(-9.95, 25.01) * mm, "end": v(-10.26, 24.76) * mm});
            skLineSegment(sketch, "E537", {"start": v(-10.26, 24.76) * mm, "end": v(-10.6, 24.5) * mm});
            skLineSegment(sketch, "E538", {"start": v(-10.6, 24.5) * mm, "end": v(-10.92, 24.26) * mm});
            skLineSegment(sketch, "E539", {"start": v(-10.92, 24.26) * mm, "end": v(-11.26, 24.03) * mm});
            skLineSegment(sketch, "E540", {"start": v(-11.26, 24.03) * mm, "end": v(-11.6, 23.8) * mm});
            skLineSegment(sketch, "E541", {"start": v(-11.6, 23.8) * mm, "end": v(-11.95, 23.6) * mm});
            skLineSegment(sketch, "E542", {"start": v(-11.95, 23.6) * mm, "end": v(-12.3, 23.39) * mm});
            skLineSegment(sketch, "E543", {"start": v(-12.3, 23.39) * mm, "end": v(-12.66, 23.19) * mm});
            skLineSegment(sketch, "E544", {"start": v(-12.66, 23.19) * mm, "end": v(-13.02, 23) * mm});
            skLineSegment(sketch, "E545", {"start": v(-13.02, 23) * mm, "end": v(-13.38, 22.82) * mm});
            skLineSegment(sketch, "E546", {"start": v(-13.38, 22.82) * mm, "end": v(-13.76, 22.65) * mm});
            skLineSegment(sketch, "E547", {"start": v(-13.76, 22.65) * mm, "end": v(-14.13, 22.49) * mm});
            skLineSegment(sketch, "E548", {"start": v(-14.13, 22.49) * mm, "end": v(-14.5, 22.34) * mm});
            skLineSegment(sketch, "E549", {"start": v(-14.5, 22.34) * mm, "end": v(-14.9, 22.2) * mm});
            skLineSegment(sketch, "E550", {"start": v(-14.9, 22.2) * mm, "end": v(-15.28, 22.06) * mm});
            skLineSegment(sketch, "E551", {"start": v(-15.28, 22.06) * mm, "end": v(-15.66, 21.94) * mm});
            skLineSegment(sketch, "E552", {"start": v(-15.66, 21.94) * mm, "end": v(-16.06, 21.83) * mm});
            skLineSegment(sketch, "E553", {"start": v(-16.06, 21.83) * mm, "end": v(-16.45, 21.72) * mm});
            skLineSegment(sketch, "E554", {"start": v(-16.45, 21.72) * mm, "end": v(-16.85, 21.63) * mm});
            skLineSegment(sketch, "E555", {"start": v(-16.85, 21.63) * mm, "end": v(-17.25, 21.54) * mm});
            skLineSegment(sketch, "E556", {"start": v(-17.25, 21.54) * mm, "end": v(-17.65, 21.47) * mm});
            skLineSegment(sketch, "E557", {"start": v(-17.65, 21.47) * mm, "end": v(-18.06, 21.4) * mm});
            skLineSegment(sketch, "E558", {"start": v(-18.06, 21.4) * mm, "end": v(-18.46, 21.35) * mm});
            skLineSegment(sketch, "E559", {"start": v(-18.46, 21.35) * mm, "end": v(-18.87, 21.3) * mm});
            skLineSegment(sketch, "E560", {"start": v(-18.87, 21.3) * mm, "end": v(-19.28, 21.27) * mm});
            skLineSegment(sketch, "E561", {"start": v(-19.28, 21.27) * mm, "end": v(-19.7, 21.25) * mm});
            skLineSegment(sketch, "E562", {"start": v(-19.7, 21.25) * mm, "end": v(-20.1, 21.23) * mm});
            skLineSegment(sketch, "E563", {"start": v(-20.1, 21.23) * mm, "end": v(-20.52, 21.23) * mm});
            skLineSegment(sketch, "E564", {"start": v(23.73, 21.23) * mm, "end": v(23.3, 21.23) * mm});
            skLineSegment(sketch, "E565", {"start": v(23.3, 21.23) * mm, "end": v(22.89, 21.24) * mm});
            skLineSegment(sketch, "E566", {"start": v(22.89, 21.24) * mm, "end": v(22.47, 21.25) * mm});
            skLineSegment(sketch, "E567", {"start": v(22.47, 21.25) * mm, "end": v(22.05, 21.28) * mm});
            skLineSegment(sketch, "E568", {"start": v(22.05, 21.28) * mm, "end": v(21.64, 21.32) * mm});
            skLineSegment(sketch, "E569", {"start": v(21.64, 21.32) * mm, "end": v(21.22, 21.37) * mm});
            skLineSegment(sketch, "E570", {"start": v(21.22, 21.37) * mm, "end": v(20.81, 21.43) * mm});
            skLineSegment(sketch, "E571", {"start": v(20.81, 21.43) * mm, "end": v(20.4, 21.5) * mm});
            skLineSegment(sketch, "E572", {"start": v(20.4, 21.5) * mm, "end": v(20, 21.58) * mm});
            skLineSegment(sketch, "E573", {"start": v(20, 21.58) * mm, "end": v(19.6, 21.67) * mm});
            skLineSegment(sketch, "E574", {"start": v(19.6, 21.67) * mm, "end": v(19.19, 21.77) * mm});
            skLineSegment(sketch, "E575", {"start": v(19.19, 21.77) * mm, "end": v(18.79, 21.88) * mm});
            skLineSegment(sketch, "E576", {"start": v(18.79, 21.88) * mm, "end": v(18.4, 22) * mm});
            skLineSegment(sketch, "E577", {"start": v(18.4, 22) * mm, "end": v(18, 22.12) * mm});
            skLineSegment(sketch, "E578", {"start": v(18, 22.12) * mm, "end": v(17.6, 22.26) * mm});
            skLineSegment(sketch, "E579", {"start": v(17.6, 22.26) * mm, "end": v(17.22, 22.41) * mm});
            skLineSegment(sketch, "E580", {"start": v(17.22, 22.41) * mm, "end": v(16.84, 22.57) * mm});
            skLineSegment(sketch, "E581", {"start": v(16.84, 22.57) * mm, "end": v(16.46, 22.74) * mm});
            skLineSegment(sketch, "E582", {"start": v(16.46, 22.74) * mm, "end": v(16.09, 22.91) * mm});
            skLineSegment(sketch, "E583", {"start": v(16.09, 22.91) * mm, "end": v(15.72, 23.1) * mm});
            skLineSegment(sketch, "E584", {"start": v(15.72, 23.1) * mm, "end": v(15.35, 23.3) * mm});
            skLineSegment(sketch, "E585", {"start": v(15.35, 23.3) * mm, "end": v(15, 23.5) * mm});
            skLineSegment(sketch, "E586", {"start": v(15, 23.5) * mm, "end": v(14.64, 23.71) * mm});
            skLineSegment(sketch, "E587", {"start": v(14.64, 23.71) * mm, "end": v(14.29, 23.93) * mm});
            skLineSegment(sketch, "E588", {"start": v(14.29, 23.93) * mm, "end": v(13.94, 24.17) * mm});
            skLineSegment(sketch, "E589", {"start": v(13.94, 24.17) * mm, "end": v(13.6, 24.4) * mm});
            skLineSegment(sketch, "E590", {"start": v(13.6, 24.4) * mm, "end": v(13.27, 24.65) * mm});
            skLineSegment(sketch, "E591", {"start": v(13.27, 24.65) * mm, "end": v(12.94, 24.91) * mm});
            skLineSegment(sketch, "E592", {"start": v(12.94, 24.91) * mm, "end": v(12.62, 25.18) * mm});
            skLineSegment(sketch, "E593", {"start": v(12.62, 25.18) * mm, "end": v(12.3, 25.45) * mm});
            skLineSegment(sketch, "E594", {"start": v(12.3, 25.45) * mm, "end": v(12, 25.73) * mm});
            skLineSegment(sketch, "E595", {"start": v(12, 25.73) * mm, "end": v(11.7, 26.03) * mm});
            skLineSegment(sketch, "E596", {"start": v(11.7, 26.03) * mm, "end": v(11.34, 26.4) * mm});
            skLineSegment(sketch, "E597", {"start": v(11.34, 26.4) * mm, "end": v(11, 26.8) * mm});
            skLineSegment(sketch, "E598", {"start": v(11, 26.8) * mm, "end": v(10.67, 27.2) * mm});
            skLineSegment(sketch, "E599", {"start": v(10.67, 27.2) * mm, "end": v(10.35, 27.6) * mm});
            skLineSegment(sketch, "E600", {"start": v(10.35, 27.6) * mm, "end": v(10.05, 28) * mm});
            skLineSegment(sketch, "E601", {"start": v(10.05, 28) * mm, "end": v(9.75, 28.42) * mm});
            skLineSegment(sketch, "E602", {"start": v(9.75, 28.42) * mm, "end": v(9.46, 28.85) * mm});
            skLineSegment(sketch, "E603", {"start": v(9.46, 28.85) * mm, "end": v(9.19, 29.28) * mm});
            skLineSegment(sketch, "E604", {"start": v(9.19, 29.28) * mm, "end": v(8.92, 29.71) * mm});
            skLineSegment(sketch, "E605", {"start": v(8.92, 29.71) * mm, "end": v(8.67, 30.16) * mm});
            skLineSegment(sketch, "E606", {"start": v(8.67, 30.16) * mm, "end": v(8.43, 30.6) * mm});
            skLineSegment(sketch, "E607", {"start": v(8.43, 30.6) * mm, "end": v(8.2, 31.06) * mm});
            skLineSegment(sketch, "E608", {"start": v(8.2, 31.06) * mm, "end": v(7.97, 31.52) * mm});
            skLineSegment(sketch, "E609", {"start": v(7.97, 31.52) * mm, "end": v(7.77, 31.98) * mm});
            skLineSegment(sketch, "E610", {"start": v(7.77, 31.98) * mm, "end": v(7.57, 32.45) * mm});
            skLineSegment(sketch, "E611", {"start": v(7.57, 32.45) * mm, "end": v(7.38, 32.93) * mm});
            skLineSegment(sketch, "E612", {"start": v(7.38, 32.93) * mm, "end": v(7.21, 33.4) * mm});
            skLineSegment(sketch, "E613", {"start": v(7.21, 33.4) * mm, "end": v(7.05, 33.89) * mm});
            skLineSegment(sketch, "E614", {"start": v(7.05, 33.89) * mm, "end": v(6.9, 34.38) * mm});
            skLineSegment(sketch, "E615", {"start": v(6.9, 34.38) * mm, "end": v(6.76, 34.87) * mm});
            skLineSegment(sketch, "E616", {"start": v(6.76, 34.87) * mm, "end": v(6.63, 35.36) * mm});
            skLineSegment(sketch, "E617", {"start": v(6.63, 35.36) * mm, "end": v(6.52, 35.86) * mm});
            skLineSegment(sketch, "E618", {"start": v(6.52, 35.86) * mm, "end": v(6.42, 36.36) * mm});
            skLineSegment(sketch, "E619", {"start": v(6.42, 36.36) * mm, "end": v(6.33, 36.86) * mm});
            skLineSegment(sketch, "E620", {"start": v(6.33, 36.86) * mm, "end": v(6.25, 37.37) * mm});
            skLineSegment(sketch, "E621", {"start": v(6.25, 37.37) * mm, "end": v(6.19, 37.87) * mm});
            skLineSegment(sketch, "E622", {"start": v(6.19, 37.87) * mm, "end": v(6.13, 38.38) * mm});
            skLineSegment(sketch, "E623", {"start": v(6.13, 38.38) * mm, "end": v(6.1, 38.9) * mm});
            skLineSegment(sketch, "E624", {"start": v(6.1, 38.9) * mm, "end": v(6.07, 39.4) * mm});
            skLineSegment(sketch, "E625", {"start": v(6.07, 39.4) * mm, "end": v(6.05, 39.92) * mm});
            skLineSegment(sketch, "E626", {"start": v(6.05, 39.92) * mm, "end": v(6.05, 40.44) * mm});
            skLineSegment(sketch, "E627", {"start": v(6.05, 40.44) * mm, "end": v(6.06, 40.96) * mm});
            skLineSegment(sketch, "E628", {"start": v(6.06, 40.96) * mm, "end": v(6.05, 41.52) * mm});
            skLineSegment(sketch, "E629", {"start": v(6.05, 41.52) * mm, "end": v(6.05, 42.08) * mm});
            skLineSegment(sketch, "E630", {"start": v(6.05, 42.08) * mm, "end": v(6.06, 42.64) * mm});
            skLineSegment(sketch, "E631", {"start": v(6.06, 42.64) * mm, "end": v(6.09, 43.2) * mm});
            skLineSegment(sketch, "E632", {"start": v(6.09, 43.2) * mm, "end": v(6.13, 43.75) * mm});
            skLineSegment(sketch, "E633", {"start": v(6.13, 43.75) * mm, "end": v(6.18, 44.3) * mm});
            skLineSegment(sketch, "E634", {"start": v(6.18, 44.3) * mm, "end": v(6.25, 44.86) * mm});
            skLineSegment(sketch, "E635", {"start": v(6.25, 44.86) * mm, "end": v(6.33, 45.4) * mm});
            skLineSegment(sketch, "E636", {"start": v(6.33, 45.4) * mm, "end": v(6.43, 45.95) * mm});
            skLineSegment(sketch, "E637", {"start": v(6.43, 45.95) * mm, "end": v(6.54, 46.5) * mm});
            skLineSegment(sketch, "E638", {"start": v(6.54, 46.5) * mm, "end": v(6.66, 47.03) * mm});
            skLineSegment(sketch, "E639", {"start": v(6.66, 47.03) * mm, "end": v(6.8, 47.57) * mm});
            skLineSegment(sketch, "E640", {"start": v(6.8, 47.57) * mm, "end": v(6.94, 48.1) * mm});
            skLineSegment(sketch, "E641", {"start": v(6.94, 48.1) * mm, "end": v(7.1, 48.63) * mm});
            skLineSegment(sketch, "E642", {"start": v(7.1, 48.63) * mm, "end": v(7.28, 49.16) * mm});
            skLineSegment(sketch, "E643", {"start": v(7.28, 49.16) * mm, "end": v(7.47, 49.68) * mm});
            skLineSegment(sketch, "E644", {"start": v(7.47, 49.68) * mm, "end": v(7.67, 50.2) * mm});
            skLineSegment(sketch, "E645", {"start": v(7.67, 50.2) * mm, "end": v(7.88, 50.7) * mm});
            skLineSegment(sketch, "E646", {"start": v(7.88, 50.7) * mm, "end": v(8.1, 51.2) * mm});
            skLineSegment(sketch, "E647", {"start": v(8.1, 51.2) * mm, "end": v(8.35, 51.7) * mm});
            skLineSegment(sketch, "E648", {"start": v(8.35, 51.7) * mm, "end": v(8.6, 52.2) * mm});
            skLineSegment(sketch, "E649", {"start": v(8.6, 52.2) * mm, "end": v(8.86, 52.69) * mm});
            skLineSegment(sketch, "E650", {"start": v(8.86, 52.69) * mm, "end": v(9.14, 53.17) * mm});
            skLineSegment(sketch, "E651", {"start": v(9.14, 53.17) * mm, "end": v(9.43, 53.64) * mm});
            skLineSegment(sketch, "E652", {"start": v(9.43, 53.64) * mm, "end": v(9.73, 54.1) * mm});
            skLineSegment(sketch, "E653", {"start": v(9.73, 54.1) * mm, "end": v(10.04, 54.57) * mm});
            skLineSegment(sketch, "E654", {"start": v(10.04, 54.57) * mm, "end": v(10.36, 55.02) * mm});
            skLineSegment(sketch, "E655", {"start": v(10.36, 55.02) * mm, "end": v(10.7, 55.47) * mm});
            skLineSegment(sketch, "E656", {"start": v(10.7, 55.47) * mm, "end": v(11.04, 55.9) * mm});
            skLineSegment(sketch, "E657", {"start": v(11.04, 55.9) * mm, "end": v(11.4, 56.33) * mm});
            skLineSegment(sketch, "E658", {"start": v(11.4, 56.33) * mm, "end": v(11.77, 56.75) * mm});
            skLineSegment(sketch, "E659", {"start": v(11.77, 56.75) * mm, "end": v(12.16, 57.16) * mm});
            skLineSegment(sketch, "E660", {"start": v(12.16, 57.16) * mm, "end": v(12.44, 57.46) * mm});
            skLineSegment(sketch, "E661", {"start": v(12.44, 57.46) * mm, "end": v(12.73, 57.74) * mm});
            skLineSegment(sketch, "E662", {"start": v(12.73, 57.74) * mm, "end": v(13.03, 58.01) * mm});
            skLineSegment(sketch, "E663", {"start": v(13.03, 58.01) * mm, "end": v(13.34, 58.28) * mm});
            skLineSegment(sketch, "E664", {"start": v(13.34, 58.28) * mm, "end": v(13.65, 58.54) * mm});
            skLineSegment(sketch, "E665", {"start": v(13.65, 58.54) * mm, "end": v(13.97, 58.78) * mm});
            skLineSegment(sketch, "E666", {"start": v(13.97, 58.78) * mm, "end": v(14.3, 59.02) * mm});
            skLineSegment(sketch, "E667", {"start": v(14.3, 59.02) * mm, "end": v(14.62, 59.26) * mm});
            skLineSegment(sketch, "E668", {"start": v(14.62, 59.26) * mm, "end": v(14.96, 59.48) * mm});
            skLineSegment(sketch, "E669", {"start": v(14.96, 59.48) * mm, "end": v(15.3, 59.7) * mm});
            skLineSegment(sketch, "E670", {"start": v(15.3, 59.7) * mm, "end": v(15.64, 59.9) * mm});
            skLineSegment(sketch, "E671", {"start": v(15.64, 59.9) * mm, "end": v(16, 60.1) * mm});
            skLineSegment(sketch, "E672", {"start": v(16, 60.1) * mm, "end": v(16.35, 60.28) * mm});
            skLineSegment(sketch, "E673", {"start": v(16.35, 60.28) * mm, "end": v(16.7, 60.46) * mm});
            skLineSegment(sketch, "E674", {"start": v(16.7, 60.46) * mm, "end": v(17.07, 60.63) * mm});
            skLineSegment(sketch, "E675", {"start": v(17.07, 60.63) * mm, "end": v(17.44, 60.78) * mm});
            skLineSegment(sketch, "E676", {"start": v(17.44, 60.78) * mm, "end": v(17.81, 60.93) * mm});
            skLineSegment(sketch, "E677", {"start": v(17.81, 60.93) * mm, "end": v(18.19, 61.07) * mm});
            skLineSegment(sketch, "E678", {"start": v(18.19, 61.07) * mm, "end": v(18.57, 61.2) * mm});
            skLineSegment(sketch, "E679", {"start": v(18.57, 61.2) * mm, "end": v(18.95, 61.33) * mm});
            skLineSegment(sketch, "E680", {"start": v(18.95, 61.33) * mm, "end": v(19.34, 61.44) * mm});
            skLineSegment(sketch, "E681", {"start": v(19.34, 61.44) * mm, "end": v(19.73, 61.54) * mm});
            skLineSegment(sketch, "E682", {"start": v(19.73, 61.54) * mm, "end": v(20.12, 61.63) * mm});
            skLineSegment(sketch, "E683", {"start": v(20.12, 61.63) * mm, "end": v(20.51, 61.71) * mm});
            skLineSegment(sketch, "E684", {"start": v(20.51, 61.71) * mm, "end": v(20.9, 61.78) * mm});
            skLineSegment(sketch, "E685", {"start": v(20.9, 61.78) * mm, "end": v(21.3, 61.84) * mm});
            skLineSegment(sketch, "E686", {"start": v(21.3, 61.84) * mm, "end": v(21.7, 61.9) * mm});
            skLineSegment(sketch, "E687", {"start": v(21.7, 61.9) * mm, "end": v(22.11, 61.93) * mm});
            skLineSegment(sketch, "E688", {"start": v(22.11, 61.93) * mm, "end": v(22.51, 61.96) * mm});
            skLineSegment(sketch, "E689", {"start": v(22.51, 61.96) * mm, "end": v(22.92, 61.98) * mm});
            skLineSegment(sketch, "E690", {"start": v(22.92, 61.98) * mm, "end": v(23.33, 62) * mm});
            skLineSegment(sketch, "E691", {"start": v(23.33, 62) * mm, "end": v(23.73, 62) * mm});
            skLineSegment(sketch, "E692", {"start": v(23.73, 62) * mm, "end": v(24.15, 61.99) * mm});
            skLineSegment(sketch, "E693", {"start": v(24.15, 61.99) * mm, "end": v(24.56, 61.97) * mm});
            skLineSegment(sketch, "E694", {"start": v(24.56, 61.97) * mm, "end": v(24.97, 61.95) * mm});
            skLineSegment(sketch, "E695", {"start": v(24.97, 61.95) * mm, "end": v(25.38, 61.91) * mm});
            skLineSegment(sketch, "E696", {"start": v(25.38, 61.91) * mm, "end": v(25.8, 61.87) * mm});
            skLineSegment(sketch, "E697", {"start": v(25.8, 61.87) * mm, "end": v(26.2, 61.8) * mm});
            skLineSegment(sketch, "E698", {"start": v(26.2, 61.8) * mm, "end": v(26.6, 61.74) * mm});
            skLineSegment(sketch, "E699", {"start": v(26.6, 61.74) * mm, "end": v(27, 61.66) * mm});
            skLineSegment(sketch, "E700", {"start": v(27, 61.66) * mm, "end": v(27.4, 61.58) * mm});
            skLineSegment(sketch, "E701", {"start": v(27.4, 61.58) * mm, "end": v(27.8, 61.48) * mm});
            skLineSegment(sketch, "E702", {"start": v(27.8, 61.48) * mm, "end": v(28.2, 61.37) * mm});
            skLineSegment(sketch, "E703", {"start": v(28.2, 61.37) * mm, "end": v(28.59, 61.25) * mm});
            skLineSegment(sketch, "E704", {"start": v(28.59, 61.25) * mm, "end": v(28.97, 61.13) * mm});
            skLineSegment(sketch, "E705", {"start": v(28.97, 61.13) * mm, "end": v(29.36, 60.99) * mm});
            skLineSegment(sketch, "E706", {"start": v(29.36, 60.99) * mm, "end": v(29.74, 60.84) * mm});
            skLineSegment(sketch, "E707", {"start": v(29.74, 60.84) * mm, "end": v(30.11, 60.68) * mm});
            skLineSegment(sketch, "E708", {"start": v(30.11, 60.68) * mm, "end": v(30.49, 60.52) * mm});
            skLineSegment(sketch, "E709", {"start": v(30.49, 60.52) * mm, "end": v(30.85, 60.34) * mm});
            skLineSegment(sketch, "E710", {"start": v(30.85, 60.34) * mm, "end": v(31.22, 60.16) * mm});
            skLineSegment(sketch, "E711", {"start": v(31.22, 60.16) * mm, "end": v(31.58, 59.96) * mm});
            skLineSegment(sketch, "E712", {"start": v(31.58, 59.96) * mm, "end": v(31.93, 59.76) * mm});
            skLineSegment(sketch, "E713", {"start": v(31.93, 59.76) * mm, "end": v(32.28, 59.55) * mm});
            skLineSegment(sketch, "E714", {"start": v(32.28, 59.55) * mm, "end": v(32.62, 59.33) * mm});
            skLineSegment(sketch, "E715", {"start": v(32.62, 59.33) * mm, "end": v(32.96, 59.1) * mm});
            skLineSegment(sketch, "E716", {"start": v(32.96, 59.1) * mm, "end": v(33.3, 58.86) * mm});
            skLineSegment(sketch, "E717", {"start": v(33.3, 58.86) * mm, "end": v(33.62, 58.6) * mm});
            skLineSegment(sketch, "E718", {"start": v(33.62, 58.6) * mm, "end": v(33.94, 58.35) * mm});
            skLineSegment(sketch, "E719", {"start": v(33.94, 58.35) * mm, "end": v(34.25, 58.09) * mm});
            skLineSegment(sketch, "E720", {"start": v(34.25, 58.09) * mm, "end": v(34.56, 57.81) * mm});
            skLineSegment(sketch, "E721", {"start": v(34.56, 57.81) * mm, "end": v(34.86, 57.53) * mm});
            skLineSegment(sketch, "E722", {"start": v(34.86, 57.53) * mm, "end": v(35.16, 57.24) * mm});
            skLineSegment(sketch, "E723", {"start": v(35.16, 57.24) * mm, "end": v(35.44, 56.94) * mm});
            skLineSegment(sketch, "E724", {"start": v(35.44, 56.94) * mm, "end": v(35.81, 56.53) * mm});
            skLineSegment(sketch, "E725", {"start": v(35.81, 56.53) * mm, "end": v(36.17, 56.11) * mm});
            skLineSegment(sketch, "E726", {"start": v(36.17, 56.11) * mm, "end": v(36.52, 55.69) * mm});
            skLineSegment(sketch, "E727", {"start": v(36.52, 55.69) * mm, "end": v(36.86, 55.25) * mm});
            skLineSegment(sketch, "E728", {"start": v(36.86, 55.25) * mm, "end": v(37.18, 54.81) * mm});
            skLineSegment(sketch, "E729", {"start": v(37.18, 54.81) * mm, "end": v(37.5, 54.36) * mm});
            skLineSegment(sketch, "E730", {"start": v(37.5, 54.36) * mm, "end": v(37.8, 53.9) * mm});
            skLineSegment(sketch, "E731", {"start": v(37.8, 53.9) * mm, "end": v(38.09, 53.44) * mm});
            skLineSegment(sketch, "E732", {"start": v(38.09, 53.44) * mm, "end": v(38.36, 52.97) * mm});
            skLineSegment(sketch, "E733", {"start": v(38.36, 52.97) * mm, "end": v(38.63, 52.5) * mm});
            skLineSegment(sketch, "E734", {"start": v(38.63, 52.5) * mm, "end": v(38.88, 52.02) * mm});
            skLineSegment(sketch, "E735", {"start": v(38.88, 52.02) * mm, "end": v(39.13, 51.53) * mm});
            skLineSegment(sketch, "E736", {"start": v(39.13, 51.53) * mm, "end": v(39.36, 51.04) * mm});
            skLineSegment(sketch, "E737", {"start": v(39.36, 51.04) * mm, "end": v(39.57, 50.54) * mm});
            skLineSegment(sketch, "E738", {"start": v(39.57, 50.54) * mm, "end": v(39.78, 50.03) * mm});
            skLineSegment(sketch, "E739", {"start": v(39.78, 50.03) * mm, "end": v(39.97, 49.52) * mm});
            skLineSegment(sketch, "E740", {"start": v(39.97, 49.52) * mm, "end": v(40.15, 49.01) * mm});
            skLineSegment(sketch, "E741", {"start": v(40.15, 49.01) * mm, "end": v(40.32, 48.5) * mm});
            skLineSegment(sketch, "E742", {"start": v(40.32, 48.5) * mm, "end": v(40.47, 47.97) * mm});
            skLineSegment(sketch, "E743", {"start": v(40.47, 47.97) * mm, "end": v(40.61, 47.45) * mm});
            skLineSegment(sketch, "E744", {"start": v(40.61, 47.45) * mm, "end": v(40.74, 46.92) * mm});
            skLineSegment(sketch, "E745", {"start": v(40.74, 46.92) * mm, "end": v(40.86, 46.38) * mm});
            skLineSegment(sketch, "E746", {"start": v(40.86, 46.38) * mm, "end": v(40.96, 45.85) * mm});
            skLineSegment(sketch, "E747", {"start": v(40.96, 45.85) * mm, "end": v(41.05, 45.3) * mm});
            skLineSegment(sketch, "E748", {"start": v(41.05, 45.3) * mm, "end": v(41.13, 44.77) * mm});
            skLineSegment(sketch, "E749", {"start": v(41.13, 44.77) * mm, "end": v(41.19, 44.23) * mm});
            skLineSegment(sketch, "E750", {"start": v(41.19, 44.23) * mm, "end": v(41.24, 43.68) * mm});
            skLineSegment(sketch, "E751", {"start": v(41.24, 43.68) * mm, "end": v(41.27, 43.13) * mm});
            skLineSegment(sketch, "E752", {"start": v(41.27, 43.13) * mm, "end": v(41.3, 42.59) * mm});
            skLineSegment(sketch, "E753", {"start": v(41.3, 42.59) * mm, "end": v(41.3, 42.04) * mm});
            skLineSegment(sketch, "E754", {"start": v(41.3, 42.04) * mm, "end": v(41.3, 41.48) * mm});
            skLineSegment(sketch, "E755", {"start": v(41.3, 41.48) * mm, "end": v(41.28, 40.93) * mm});
            skLineSegment(sketch, "E756", {"start": v(41.28, 40.93) * mm, "end": v(41.29, 40.42) * mm});
            skLineSegment(sketch, "E757", {"start": v(41.29, 40.42) * mm, "end": v(41.28, 39.9) * mm});
            skLineSegment(sketch, "E758", {"start": v(41.28, 39.9) * mm, "end": v(41.26, 39.4) * mm});
            skLineSegment(sketch, "E759", {"start": v(41.26, 39.4) * mm, "end": v(41.23, 38.88) * mm});
            skLineSegment(sketch, "E760", {"start": v(41.23, 38.88) * mm, "end": v(41.2, 38.37) * mm});
            skLineSegment(sketch, "E761", {"start": v(41.2, 38.37) * mm, "end": v(41.13, 37.86) * mm});
            skLineSegment(sketch, "E762", {"start": v(41.13, 37.86) * mm, "end": v(41.07, 37.36) * mm});
            skLineSegment(sketch, "E763", {"start": v(41.07, 37.36) * mm, "end": v(40.98, 36.86) * mm});
            skLineSegment(sketch, "E764", {"start": v(40.98, 36.86) * mm, "end": v(40.9, 36.36) * mm});
            skLineSegment(sketch, "E765", {"start": v(40.9, 36.36) * mm, "end": v(40.78, 35.86) * mm});
            skLineSegment(sketch, "E766", {"start": v(40.78, 35.86) * mm, "end": v(40.67, 35.36) * mm});
            skLineSegment(sketch, "E767", {"start": v(40.67, 35.36) * mm, "end": v(40.54, 34.87) * mm});
            skLineSegment(sketch, "E768", {"start": v(40.54, 34.87) * mm, "end": v(40.4, 34.39) * mm});
            skLineSegment(sketch, "E769", {"start": v(40.4, 34.39) * mm, "end": v(40.24, 33.9) * mm});
            skLineSegment(sketch, "E770", {"start": v(40.24, 33.9) * mm, "end": v(40.07, 33.42) * mm});
            skLineSegment(sketch, "E771", {"start": v(40.07, 33.42) * mm, "end": v(39.9, 32.95) * mm});
            skLineSegment(sketch, "E772", {"start": v(39.9, 32.95) * mm, "end": v(39.7, 32.48) * mm});
            skLineSegment(sketch, "E773", {"start": v(39.7, 32.48) * mm, "end": v(39.5, 32.01) * mm});
            skLineSegment(sketch, "E774", {"start": v(39.5, 32.01) * mm, "end": v(39.3, 31.55) * mm});
            skLineSegment(sketch, "E775", {"start": v(39.3, 31.55) * mm, "end": v(39.07, 31.1) * mm});
            skLineSegment(sketch, "E776", {"start": v(39.07, 31.1) * mm, "end": v(38.83, 30.65) * mm});
            skLineSegment(sketch, "E777", {"start": v(38.83, 30.65) * mm, "end": v(38.58, 30.2) * mm});
            skLineSegment(sketch, "E778", {"start": v(38.58, 30.2) * mm, "end": v(38.33, 29.76) * mm});
            skLineSegment(sketch, "E779", {"start": v(38.33, 29.76) * mm, "end": v(38.06, 29.33) * mm});
            skLineSegment(sketch, "E780", {"start": v(38.06, 29.33) * mm, "end": v(37.78, 28.9) * mm});
            skLineSegment(sketch, "E781", {"start": v(37.78, 28.9) * mm, "end": v(37.48, 28.49) * mm});
            skLineSegment(sketch, "E782", {"start": v(37.48, 28.49) * mm, "end": v(37.18, 28.08) * mm});
            skLineSegment(sketch, "E783", {"start": v(37.18, 28.08) * mm, "end": v(36.87, 27.67) * mm});
            skLineSegment(sketch, "E784", {"start": v(36.87, 27.67) * mm, "end": v(36.55, 27.27) * mm});
            skLineSegment(sketch, "E785", {"start": v(36.55, 27.27) * mm, "end": v(36.21, 26.89) * mm});
            skLineSegment(sketch, "E786", {"start": v(36.21, 26.89) * mm, "end": v(35.87, 26.5) * mm});
            skLineSegment(sketch, "E787", {"start": v(35.87, 26.5) * mm, "end": v(35.52, 26.13) * mm});
            skLineSegment(sketch, "E788", {"start": v(35.52, 26.13) * mm, "end": v(35.22, 25.84) * mm});
            skLineSegment(sketch, "E789", {"start": v(35.22, 25.84) * mm, "end": v(34.92, 25.56) * mm});
            skLineSegment(sketch, "E790", {"start": v(34.92, 25.56) * mm, "end": v(34.61, 25.28) * mm});
            skLineSegment(sketch, "E791", {"start": v(34.61, 25.28) * mm, "end": v(34.3, 25.01) * mm});
            skLineSegment(sketch, "E792", {"start": v(34.3, 25.01) * mm, "end": v(33.98, 24.76) * mm});
            skLineSegment(sketch, "E793", {"start": v(33.98, 24.76) * mm, "end": v(33.66, 24.5) * mm});
            skLineSegment(sketch, "E794", {"start": v(33.66, 24.5) * mm, "end": v(33.32, 24.26) * mm});
            skLineSegment(sketch, "E795", {"start": v(33.32, 24.26) * mm, "end": v(32.99, 24.03) * mm});
            skLineSegment(sketch, "E796", {"start": v(32.99, 24.03) * mm, "end": v(32.65, 23.8) * mm});
            skLineSegment(sketch, "E797", {"start": v(32.65, 23.8) * mm, "end": v(32.3, 23.6) * mm});
            skLineSegment(sketch, "E798", {"start": v(32.3, 23.6) * mm, "end": v(31.95, 23.39) * mm});
            skLineSegment(sketch, "E799", {"start": v(31.95, 23.39) * mm, "end": v(31.59, 23.19) * mm});
            skLineSegment(sketch, "E800", {"start": v(31.59, 23.19) * mm, "end": v(31.23, 23) * mm});
            skLineSegment(sketch, "E801", {"start": v(31.23, 23) * mm, "end": v(30.86, 22.82) * mm});
            skLineSegment(sketch, "E802", {"start": v(30.86, 22.82) * mm, "end": v(30.49, 22.65) * mm});
            skLineSegment(sketch, "E803", {"start": v(30.49, 22.65) * mm, "end": v(30.12, 22.49) * mm});
            skLineSegment(sketch, "E804", {"start": v(30.12, 22.49) * mm, "end": v(29.74, 22.34) * mm});
            skLineSegment(sketch, "E805", {"start": v(29.74, 22.34) * mm, "end": v(29.36, 22.2) * mm});
            skLineSegment(sketch, "E806", {"start": v(29.36, 22.2) * mm, "end": v(28.97, 22.06) * mm});
            skLineSegment(sketch, "E807", {"start": v(28.97, 22.06) * mm, "end": v(28.58, 21.94) * mm});
            skLineSegment(sketch, "E808", {"start": v(28.58, 21.94) * mm, "end": v(28.19, 21.83) * mm});
            skLineSegment(sketch, "E809", {"start": v(28.19, 21.83) * mm, "end": v(27.8, 21.72) * mm});
            skLineSegment(sketch, "E810", {"start": v(27.8, 21.72) * mm, "end": v(27.4, 21.63) * mm});
            skLineSegment(sketch, "E811", {"start": v(27.4, 21.63) * mm, "end": v(27, 21.54) * mm});
            skLineSegment(sketch, "E812", {"start": v(27, 21.54) * mm, "end": v(26.6, 21.47) * mm});
            skLineSegment(sketch, "E813", {"start": v(26.6, 21.47) * mm, "end": v(26.19, 21.4) * mm});
            skLineSegment(sketch, "E814", {"start": v(26.19, 21.4) * mm, "end": v(25.78, 21.35) * mm});
            skLineSegment(sketch, "E815", {"start": v(25.78, 21.35) * mm, "end": v(25.37, 21.3) * mm});
            skLineSegment(sketch, "E816", {"start": v(25.37, 21.3) * mm, "end": v(24.96, 21.27) * mm});
            skLineSegment(sketch, "E817", {"start": v(24.96, 21.27) * mm, "end": v(24.55, 21.25) * mm});
            skLineSegment(sketch, "E818", {"start": v(24.55, 21.25) * mm, "end": v(24.14, 21.23) * mm});
            skLineSegment(sketch, "E819", {"start": v(24.14, 21.23) * mm, "end": v(23.73, 21.23) * mm});
            skLineSegment(sketch, "E820", {"start": v(50.3, 21.8) * mm, "end": v(50.3, 61.75) * mm});
            skLineSegment(sketch, "E821", {"start": v(50.3, 61.75) * mm, "end": v(67.86, 61.75) * mm});
            skLineSegment(sketch, "E822", {"start": v(67.86, 61.75) * mm, "end": v(68.35, 61.75) * mm});
            skLineSegment(sketch, "E823", {"start": v(68.35, 61.75) * mm, "end": v(68.85, 61.72) * mm});
            skLineSegment(sketch, "E824", {"start": v(68.85, 61.72) * mm, "end": v(69.33, 61.66) * mm});
            skLineSegment(sketch, "E825", {"start": v(69.33, 61.66) * mm, "end": v(69.82, 61.59) * mm});
            skLineSegment(sketch, "E826", {"start": v(69.82, 61.59) * mm, "end": v(70.3, 61.48) * mm});
            skLineSegment(sketch, "E827", {"start": v(70.3, 61.48) * mm, "end": v(70.76, 61.36) * mm});
            skLineSegment(sketch, "E828", {"start": v(70.76, 61.36) * mm, "end": v(71.23, 61.2) * mm});
            skLineSegment(sketch, "E829", {"start": v(71.23, 61.2) * mm, "end": v(71.68, 61.03) * mm});
            skLineSegment(sketch, "E830", {"start": v(71.68, 61.03) * mm, "end": v(72.13, 60.83) * mm});
            skLineSegment(sketch, "E831", {"start": v(72.13, 60.83) * mm, "end": v(72.56, 60.61) * mm});
            skLineSegment(sketch, "E832", {"start": v(72.56, 60.61) * mm, "end": v(72.99, 60.37) * mm});
            skLineSegment(sketch, "E833", {"start": v(72.99, 60.37) * mm, "end": v(73.4, 60.11) * mm});
            skLineSegment(sketch, "E834", {"start": v(73.4, 60.11) * mm, "end": v(73.8, 59.83) * mm});
            skLineSegment(sketch, "E835", {"start": v(73.8, 59.83) * mm, "end": v(74.18, 59.52) * mm});
            skLineSegment(sketch, "E836", {"start": v(74.18, 59.52) * mm, "end": v(74.55, 59.2) * mm});
            skLineSegment(sketch, "E837", {"start": v(74.55, 59.2) * mm, "end": v(74.9, 58.85) * mm});
            skLineSegment(sketch, "E838", {"start": v(74.9, 58.85) * mm, "end": v(75.24, 58.5) * mm});
            skLineSegment(sketch, "E839", {"start": v(75.24, 58.5) * mm, "end": v(75.56, 58.13) * mm});
            skLineSegment(sketch, "E840", {"start": v(75.56, 58.13) * mm, "end": v(75.86, 57.75) * mm});
            skLineSegment(sketch, "E841", {"start": v(75.86, 57.75) * mm, "end": v(76.15, 57.35) * mm});
            skLineSegment(sketch, "E842", {"start": v(76.15, 57.35) * mm, "end": v(76.4, 56.95) * mm});
            skLineSegment(sketch, "E843", {"start": v(76.4, 56.95) * mm, "end": v(76.65, 56.53) * mm});
            skLineSegment(sketch, "E844", {"start": v(76.65, 56.53) * mm, "end": v(76.87, 56.1) * mm});
            skLineSegment(sketch, "E845", {"start": v(76.87, 56.1) * mm, "end": v(77.06, 55.66) * mm});
            skLineSegment(sketch, "E846", {"start": v(77.06, 55.66) * mm, "end": v(77.24, 55.2) * mm});
            skLineSegment(sketch, "E847", {"start": v(77.24, 55.2) * mm, "end": v(77.4, 54.75) * mm});
            skLineSegment(sketch, "E848", {"start": v(77.4, 54.75) * mm, "end": v(77.52, 54.28) * mm});
            skLineSegment(sketch, "E849", {"start": v(77.52, 54.28) * mm, "end": v(77.63, 53.8) * mm});
            skLineSegment(sketch, "E850", {"start": v(77.63, 53.8) * mm, "end": v(77.71, 53.33) * mm});
            skLineSegment(sketch, "E851", {"start": v(77.71, 53.33) * mm, "end": v(77.77, 52.85) * mm});
            skLineSegment(sketch, "E852", {"start": v(77.77, 52.85) * mm, "end": v(77.8, 52.36) * mm});
            skLineSegment(sketch, "E853", {"start": v(77.8, 52.36) * mm, "end": v(77.82, 51.87) * mm});
            skLineSegment(sketch, "E854", {"start": v(77.82, 51.87) * mm, "end": v(77.82, 51.37) * mm});
            skLineSegment(sketch, "E855", {"start": v(77.82, 51.37) * mm, "end": v(77.8, 50.87) * mm});
            skLineSegment(sketch, "E856", {"start": v(77.8, 50.87) * mm, "end": v(77.75, 50.38) * mm});
            skLineSegment(sketch, "E857", {"start": v(77.75, 50.38) * mm, "end": v(77.68, 49.89) * mm});
            skLineSegment(sketch, "E858", {"start": v(77.68, 49.89) * mm, "end": v(77.58, 49.4) * mm});
            skLineSegment(sketch, "E859", {"start": v(77.58, 49.4) * mm, "end": v(77.46, 48.92) * mm});
            skLineSegment(sketch, "E860", {"start": v(77.46, 48.92) * mm, "end": v(77.31, 48.45) * mm});
            skLineSegment(sketch, "E861", {"start": v(77.31, 48.45) * mm, "end": v(77.14, 47.98) * mm});
            skLineSegment(sketch, "E862", {"start": v(77.14, 47.98) * mm, "end": v(76.95, 47.53) * mm});
            skLineSegment(sketch, "E863", {"start": v(76.95, 47.53) * mm, "end": v(76.73, 47.08) * mm});
            skLineSegment(sketch, "E864", {"start": v(76.73, 47.08) * mm, "end": v(76.5, 46.65) * mm});
            skLineSegment(sketch, "E865", {"start": v(76.5, 46.65) * mm, "end": v(76.23, 46.23) * mm});
            skLineSegment(sketch, "E866", {"start": v(76.23, 46.23) * mm, "end": v(75.95, 45.82) * mm});
            skLineSegment(sketch, "E867", {"start": v(75.95, 45.82) * mm, "end": v(75.65, 45.42) * mm});
            skLineSegment(sketch, "E868", {"start": v(75.65, 45.42) * mm, "end": v(75.33, 45.04) * mm});
            skLineSegment(sketch, "E869", {"start": v(75.33, 45.04) * mm, "end": v(74.98, 44.68) * mm});
            skLineSegment(sketch, "E870", {"start": v(74.98, 44.68) * mm, "end": v(74.62, 44.34) * mm});
            skLineSegment(sketch, "E871", {"start": v(74.62, 44.34) * mm, "end": v(74.25, 44.01) * mm});
            skLineSegment(sketch, "E872", {"start": v(74.25, 44.01) * mm, "end": v(73.86, 43.7) * mm});
            skLineSegment(sketch, "E873", {"start": v(73.86, 43.7) * mm, "end": v(73.45, 43.42) * mm});
            skLineSegment(sketch, "E874", {"start": v(73.45, 43.42) * mm, "end": v(73.03, 43.16) * mm});
            skLineSegment(sketch, "E875", {"start": v(73.03, 43.16) * mm, "end": v(72.6, 42.92) * mm});
            skLineSegment(sketch, "E876", {"start": v(72.6, 42.92) * mm, "end": v(72.16, 42.7) * mm});
            skLineSegment(sketch, "E877", {"start": v(72.16, 42.7) * mm, "end": v(71.71, 42.5) * mm});
            skLineSegment(sketch, "E878", {"start": v(71.71, 42.5) * mm, "end": v(71.26, 42.33) * mm});
            skLineSegment(sketch, "E879", {"start": v(71.26, 42.33) * mm, "end": v(70.79, 42.18) * mm});
            skLineSegment(sketch, "E880", {"start": v(70.79, 42.18) * mm, "end": v(70.31, 42.05) * mm});
            skLineSegment(sketch, "E881", {"start": v(70.31, 42.05) * mm, "end": v(69.83, 41.95) * mm});
            skLineSegment(sketch, "E882", {"start": v(69.83, 41.95) * mm, "end": v(69.34, 41.87) * mm});
            skLineSegment(sketch, "E883", {"start": v(69.34, 41.87) * mm, "end": v(68.85, 41.82) * mm});
            skLineSegment(sketch, "E884", {"start": v(68.85, 41.82) * mm, "end": v(68.36, 41.79) * mm});
            skLineSegment(sketch, "E885", {"start": v(68.36, 41.79) * mm, "end": v(67.86, 41.78) * mm});
            skLineSegment(sketch, "E886", {"start": v(67.86, 41.78) * mm, "end": v(50.3, 41.78) * mm});
            skLineSegment(sketch, "E887", {"start": v(67.86, 41.78) * mm, "end": v(68.27, 41.78) * mm});
            skLineSegment(sketch, "E888", {"start": v(68.27, 41.78) * mm, "end": v(68.68, 41.76) * mm});
            skLineSegment(sketch, "E889", {"start": v(68.68, 41.76) * mm, "end": v(69.08, 41.71) * mm});
            skLineSegment(sketch, "E890", {"start": v(69.08, 41.71) * mm, "end": v(69.48, 41.65) * mm});
            skLineSegment(sketch, "E891", {"start": v(69.48, 41.65) * mm, "end": v(69.88, 41.56) * mm});
            skLineSegment(sketch, "E892", {"start": v(69.88, 41.56) * mm, "end": v(70.27, 41.46) * mm});
            skLineSegment(sketch, "E893", {"start": v(70.27, 41.46) * mm, "end": v(70.65, 41.34) * mm});
            skLineSegment(sketch, "E894", {"start": v(70.65, 41.34) * mm, "end": v(71.03, 41.2) * mm});
            skLineSegment(sketch, "E895", {"start": v(71.03, 41.2) * mm, "end": v(71.4, 41.03) * mm});
            skLineSegment(sketch, "E896", {"start": v(71.4, 41.03) * mm, "end": v(71.76, 40.85) * mm});
            skLineSegment(sketch, "E897", {"start": v(71.76, 40.85) * mm, "end": v(72.11, 40.65) * mm});
            skLineSegment(sketch, "E898", {"start": v(72.11, 40.65) * mm, "end": v(72.46, 40.44) * mm});
            skLineSegment(sketch, "E899", {"start": v(72.46, 40.44) * mm, "end": v(72.79, 40.2) * mm});
            skLineSegment(sketch, "E900", {"start": v(72.79, 40.2) * mm, "end": v(73.1, 39.95) * mm});
            skLineSegment(sketch, "E901", {"start": v(73.1, 39.95) * mm, "end": v(73.42, 39.68) * mm});
            skLineSegment(sketch, "E902", {"start": v(73.42, 39.68) * mm, "end": v(73.7, 39.4) * mm});
            skLineSegment(sketch, "E903", {"start": v(73.7, 39.4) * mm, "end": v(74.05, 38.9) * mm});
            skLineSegment(sketch, "E904", {"start": v(74.05, 38.9) * mm, "end": v(74.37, 38.38) * mm});
            skLineSegment(sketch, "E905", {"start": v(74.37, 38.38) * mm, "end": v(74.66, 37.86) * mm});
            skLineSegment(sketch, "E906", {"start": v(74.66, 37.86) * mm, "end": v(74.93, 37.32) * mm});
            skLineSegment(sketch, "E907", {"start": v(74.93, 37.32) * mm, "end": v(75.18, 36.77) * mm});
            skLineSegment(sketch, "E908", {"start": v(75.18, 36.77) * mm, "end": v(75.4, 36.22) * mm});
            skLineSegment(sketch, "E909", {"start": v(75.4, 36.22) * mm, "end": v(75.59, 35.65) * mm});
            skLineSegment(sketch, "E910", {"start": v(75.59, 35.65) * mm, "end": v(75.76, 35.08) * mm});
            skLineSegment(sketch, "E911", {"start": v(75.76, 35.08) * mm, "end": v(75.9, 34.5) * mm});
            skLineSegment(sketch, "E912", {"start": v(75.9, 34.5) * mm, "end": v(76.02, 33.9) * mm});
            skLineSegment(sketch, "E913", {"start": v(76.02, 33.9) * mm, "end": v(76.11, 33.32) * mm});
            skLineSegment(sketch, "E914", {"start": v(76.11, 33.32) * mm, "end": v(76.18, 32.72) * mm});
            skLineSegment(sketch, "E915", {"start": v(76.18, 32.72) * mm, "end": v(76.22, 32.12) * mm});
            skLineSegment(sketch, "E916", {"start": v(76.22, 32.12) * mm, "end": v(76.23, 31.52) * mm});
            skLineSegment(sketch, "E917", {"start": v(76.23, 31.52) * mm, "end": v(76.21, 30.91) * mm});
            skLineSegment(sketch, "E918", {"start": v(76.21, 30.91) * mm, "end": v(76.17, 30.31) * mm});
            skLineSegment(sketch, "E919", {"start": v(76.17, 30.31) * mm, "end": v(76.16, 29.77) * mm});
            skLineSegment(sketch, "E920", {"start": v(76.16, 29.77) * mm, "end": v(76.16, 29.24) * mm});
            skLineSegment(sketch, "E921", {"start": v(76.16, 29.24) * mm, "end": v(76.18, 28.7) * mm});
            skLineSegment(sketch, "E922", {"start": v(76.18, 28.7) * mm, "end": v(76.2, 28.16) * mm});
            skLineSegment(sketch, "E923", {"start": v(76.2, 28.16) * mm, "end": v(76.23, 27.62) * mm});
            skLineSegment(sketch, "E924", {"start": v(76.23, 27.62) * mm, "end": v(76.27, 27.09) * mm});
            skLineSegment(sketch, "E925", {"start": v(76.27, 27.09) * mm, "end": v(76.32, 26.55) * mm});
            skLineSegment(sketch, "E926", {"start": v(76.32, 26.55) * mm, "end": v(76.38, 26.01) * mm});
            skLineSegment(sketch, "E927", {"start": v(76.38, 26.01) * mm, "end": v(76.45, 25.48) * mm});
            skLineSegment(sketch, "E928", {"start": v(76.45, 25.48) * mm, "end": v(76.53, 24.95) * mm});
            skLineSegment(sketch, "E929", {"start": v(76.53, 24.95) * mm, "end": v(76.62, 24.42) * mm});
            skLineSegment(sketch, "E930", {"start": v(76.62, 24.42) * mm, "end": v(76.71, 23.89) * mm});
            skLineSegment(sketch, "E931", {"start": v(76.71, 23.89) * mm, "end": v(76.82, 23.36) * mm});
            skLineSegment(sketch, "E932", {"start": v(76.82, 23.36) * mm, "end": v(76.94, 22.83) * mm});
            skLineSegment(sketch, "E933", {"start": v(76.94, 22.83) * mm, "end": v(77.07, 22.31) * mm});
            skLineSegment(sketch, "E934", {"start": v(77.07, 22.31) * mm, "end": v(77.2, 21.8) * mm});
            skLineSegment(sketch, "E935", {"start": v(112.94, 55.07) * mm, "end": v(113.53, 55.08) * mm});
            skLineSegment(sketch, "E936", {"start": v(113.53, 55.08) * mm, "end": v(114.11, 55.1) * mm});
            skLineSegment(sketch, "E937", {"start": v(114.11, 55.1) * mm, "end": v(114.69, 55.15) * mm});
            skLineSegment(sketch, "E938", {"start": v(114.69, 55.15) * mm, "end": v(115.25, 55.2) * mm});
            skLineSegment(sketch, "E939", {"start": v(115.25, 55.2) * mm, "end": v(115.8, 55.28) * mm});
            skLineSegment(sketch, "E940", {"start": v(115.8, 55.28) * mm, "end": v(116.35, 55.37) * mm});
            skLineSegment(sketch, "E941", {"start": v(116.35, 55.37) * mm, "end": v(116.89, 55.48) * mm});
            skLineSegment(sketch, "E942", {"start": v(116.89, 55.48) * mm, "end": v(117.41, 55.6) * mm});
            skLineSegment(sketch, "E943", {"start": v(117.41, 55.6) * mm, "end": v(117.92, 55.73) * mm});
            skLineSegment(sketch, "E944", {"start": v(117.92, 55.73) * mm, "end": v(118.41, 55.88) * mm});
            skLineSegment(sketch, "E945", {"start": v(118.41, 55.88) * mm, "end": v(118.9, 56.04) * mm});
            skLineSegment(sketch, "E946", {"start": v(118.9, 56.04) * mm, "end": v(119.36, 56.22) * mm});
            skLineSegment(sketch, "E947", {"start": v(119.36, 56.22) * mm, "end": v(119.81, 56.4) * mm});
            skLineSegment(sketch, "E948", {"start": v(119.81, 56.4) * mm, "end": v(120.25, 56.6) * mm});
            skLineSegment(sketch, "E949", {"start": v(120.25, 56.6) * mm, "end": v(120.66, 56.82) * mm});
            skLineSegment(sketch, "E950", {"start": v(120.66, 56.82) * mm, "end": v(121.06, 57.04) * mm});
            skLineSegment(sketch, "E951", {"start": v(121.06, 57.04) * mm, "end": v(121.44, 57.27) * mm});
            skLineSegment(sketch, "E952", {"start": v(121.44, 57.27) * mm, "end": v(121.8, 57.52) * mm});
            skLineSegment(sketch, "E953", {"start": v(121.8, 57.52) * mm, "end": v(122.15, 57.77) * mm});
            skLineSegment(sketch, "E954", {"start": v(122.15, 57.77) * mm, "end": v(122.47, 58.03) * mm});
            skLineSegment(sketch, "E955", {"start": v(122.47, 58.03) * mm, "end": v(122.77, 58.3) * mm});
            skLineSegment(sketch, "E956", {"start": v(122.77, 58.3) * mm, "end": v(123.04, 58.59) * mm});
            skLineSegment(sketch, "E957", {"start": v(123.04, 58.59) * mm, "end": v(123.3, 58.88) * mm});
            skLineSegment(sketch, "E958", {"start": v(123.3, 58.88) * mm, "end": v(123.53, 59.18) * mm});
            skLineSegment(sketch, "E959", {"start": v(123.53, 59.18) * mm, "end": v(123.73, 59.48) * mm});
            skLineSegment(sketch, "E960", {"start": v(123.73, 59.48) * mm, "end": v(123.91, 59.8) * mm});
            skLineSegment(sketch, "E961", {"start": v(123.91, 59.8) * mm, "end": v(124.07, 60.11) * mm});
            skLineSegment(sketch, "E962", {"start": v(124.07, 60.11) * mm, "end": v(124.2, 60.44) * mm});
            skLineSegment(sketch, "E963", {"start": v(124.2, 60.44) * mm, "end": v(124.3, 60.77) * mm});
            skLineSegment(sketch, "E964", {"start": v(124.3, 60.77) * mm, "end": v(124.37, 61.1) * mm});
            skLineSegment(sketch, "E965", {"start": v(124.37, 61.1) * mm, "end": v(124.41, 61.45) * mm});
            skLineSegment(sketch, "E966", {"start": v(124.41, 61.45) * mm, "end": v(124.43, 61.62) * mm});
            skLineSegment(sketch, "E967", {"start": v(124.43, 61.62) * mm, "end": v(124.43, 61.8) * mm});
            skLineSegment(sketch, "E968", {"start": v(124.43, 61.8) * mm, "end": v(125.07, 61.8) * mm});
            skLineSegment(sketch, "E969", {"start": v(125.07, 61.8) * mm, "end": v(125.07, 21.8) * mm});
            skArc(sketch, "E970", {"start": v(576.08, 1161.23) * mm, "mid": v(574.98, 1163.88) * mm, "end": v(572.33, 1164.98) * mm});
            skArc(sketch, "E971", {"start": v(572.33, 1164.98) * mm, "mid": v(569.68, 1163.88) * mm, "end": v(568.58, 1161.23) * mm});
            skArc(sketch, "E972", {"start": v(568.58, 1161.23) * mm, "mid": v(569.68, 1158.58) * mm, "end": v(572.33, 1157.48) * mm});
            skArc(sketch, "E973", {"start": v(572.33, 1157.48) * mm, "mid": v(574.98, 1158.58) * mm, "end": v(576.08, 1161.23) * mm});
            skArc(sketch, "E974", {"start": v(576.08, 924.6) * mm, "mid": v(574.98, 927.26) * mm, "end": v(572.33, 928.36) * mm});
            skArc(sketch, "E975", {"start": v(572.33, 928.36) * mm, "mid": v(569.68, 927.26) * mm, "end": v(568.58, 924.6) * mm});
            skArc(sketch, "E976", {"start": v(568.58, 924.6) * mm, "mid": v(569.68, 921.96) * mm, "end": v(572.33, 920.86) * mm});
            skArc(sketch, "E977", {"start": v(572.33, 920.86) * mm, "mid": v(574.98, 921.96) * mm, "end": v(576.08, 924.6) * mm});
            skArc(sketch, "E978", {"start": v(576.08, 854.1) * mm, "mid": v(574.98, 856.75) * mm, "end": v(572.33, 857.85) * mm});
            skArc(sketch, "E979", {"start": v(572.33, 857.85) * mm, "mid": v(569.68, 856.75) * mm, "end": v(568.58, 854.1) * mm});
            skArc(sketch, "E980", {"start": v(568.58, 854.1) * mm, "mid": v(569.68, 851.45) * mm, "end": v(572.33, 850.35) * mm});
            skArc(sketch, "E981", {"start": v(572.33, 850.35) * mm, "mid": v(574.98, 851.45) * mm, "end": v(576.08, 854.1) * mm});
            skArc(sketch, "E982", {"start": v(576.08, 1041.06) * mm, "mid": v(574.98, 1043.72) * mm, "end": v(572.33, 1044.81) * mm});
            skArc(sketch, "E983", {"start": v(572.33, 1044.81) * mm, "mid": v(569.68, 1043.72) * mm, "end": v(568.58, 1041.06) * mm});
            skArc(sketch, "E984", {"start": v(568.58, 1041.06) * mm, "mid": v(569.68, 1038.41) * mm, "end": v(572.33, 1037.31) * mm});
            skArc(sketch, "E985", {"start": v(572.33, 1037.31) * mm, "mid": v(574.98, 1038.41) * mm, "end": v(576.08, 1041.06) * mm});
            skArc(sketch, "E986", {"start": v(576.08, 589.45) * mm, "mid": v(574.98, 592.1) * mm, "end": v(572.33, 593.2) * mm});
            skArc(sketch, "E987", {"start": v(572.33, 593.2) * mm, "mid": v(569.68, 592.1) * mm, "end": v(568.58, 589.45) * mm});
            skArc(sketch, "E988", {"start": v(568.58, 589.45) * mm, "mid": v(569.68, 586.8) * mm, "end": v(572.33, 585.7) * mm});
            skArc(sketch, "E989", {"start": v(572.33, 585.7) * mm, "mid": v(574.98, 586.8) * mm, "end": v(576.08, 589.45) * mm});
            skArc(sketch, "E990", {"start": v(576.08, 729.1) * mm, "mid": v(574.98, 731.75) * mm, "end": v(572.33, 732.85) * mm});
            skArc(sketch, "E991", {"start": v(572.33, 732.85) * mm, "mid": v(569.68, 731.75) * mm, "end": v(568.58, 729.1) * mm});
            skArc(sketch, "E992", {"start": v(568.58, 729.1) * mm, "mid": v(569.68, 726.45) * mm, "end": v(572.33, 725.35) * mm});
            skArc(sketch, "E993", {"start": v(572.33, 725.35) * mm, "mid": v(574.98, 726.45) * mm, "end": v(576.08, 729.1) * mm});
            skArc(sketch, "E994", {"start": v(576.08, 439.45) * mm, "mid": v(574.98, 442.1) * mm, "end": v(572.33, 443.2) * mm});
            skArc(sketch, "E995", {"start": v(572.33, 443.2) * mm, "mid": v(569.68, 442.1) * mm, "end": v(568.58, 439.45) * mm});
            skArc(sketch, "E996", {"start": v(568.58, 439.45) * mm, "mid": v(569.68, 436.8) * mm, "end": v(572.33, 435.7) * mm});
            skArc(sketch, "E997", {"start": v(572.33, 435.7) * mm, "mid": v(574.98, 436.8) * mm, "end": v(576.08, 439.45) * mm});
            skArc(sketch, "E998", {"start": v(576.08, 289.45) * mm, "mid": v(574.98, 292.1) * mm, "end": v(572.33, 293.2) * mm});
            skArc(sketch, "E999", {"start": v(572.33, 293.2) * mm, "mid": v(569.68, 292.1) * mm, "end": v(568.58, 289.45) * mm});
            skArc(sketch, "E1000", {"start": v(568.58, 289.45) * mm, "mid": v(569.68, 286.8) * mm, "end": v(572.33, 285.7) * mm});
            skArc(sketch, "E1001", {"start": v(572.33, 285.7) * mm, "mid": v(574.98, 286.8) * mm, "end": v(576.08, 289.45) * mm});
            skArc(sketch, "E1002", {"start": v(576.08, 167.99) * mm, "mid": v(574.98, 170.64) * mm, "end": v(572.33, 171.74) * mm});
            skArc(sketch, "E1003", {"start": v(572.33, 171.74) * mm, "mid": v(569.68, 170.64) * mm, "end": v(568.58, 167.99) * mm});
            skArc(sketch, "E1004", {"start": v(568.58, 167.99) * mm, "mid": v(569.68, 165.34) * mm, "end": v(572.33, 164.24) * mm});
            skArc(sketch, "E1005", {"start": v(572.33, 164.24) * mm, "mid": v(574.98, 165.34) * mm, "end": v(576.08, 167.99) * mm});
            skArc(sketch, "E1006", {"start": v(576.08, 46.3) * mm, "mid": v(574.98, 48.95) * mm, "end": v(572.33, 50.05) * mm});
            skArc(sketch, "E1007", {"start": v(572.33, 50.05) * mm, "mid": v(569.68, 48.95) * mm, "end": v(568.58, 46.3) * mm});
            skArc(sketch, "E1008", {"start": v(568.58, 46.3) * mm, "mid": v(569.68, 43.65) * mm, "end": v(572.33, 42.55) * mm});
            skArc(sketch, "E1009", {"start": v(572.33, 42.55) * mm, "mid": v(574.98, 43.65) * mm, "end": v(576.08, 46.3) * mm});
            skArc(sketch, "E1010", {"start": v(576.08, -197.02) * mm, "mid": v(574.98, -194.36) * mm, "end": v(572.33, -193.27) * mm});
            skArc(sketch, "E1011", {"start": v(572.33, -193.27) * mm, "mid": v(569.68, -194.36) * mm, "end": v(568.58, -197.02) * mm});
            skArc(sketch, "E1012", {"start": v(568.58, -197.02) * mm, "mid": v(569.68, -199.67) * mm, "end": v(572.33, -200.77) * mm});
            skArc(sketch, "E1013", {"start": v(572.33, -200.77) * mm, "mid": v(574.98, -199.67) * mm, "end": v(576.08, -197.02) * mm});
            skArc(sketch, "E1014", {"start": v(576.08, -77.47) * mm, "mid": v(574.98, -74.82) * mm, "end": v(572.33, -73.72) * mm});
            skArc(sketch, "E1015", {"start": v(572.33, -73.72) * mm, "mid": v(569.68, -74.82) * mm, "end": v(568.58, -77.47) * mm});
            skArc(sketch, "E1016", {"start": v(568.58, -77.47) * mm, "mid": v(569.68, -80.12) * mm, "end": v(572.33, -81.22) * mm});
            skArc(sketch, "E1017", {"start": v(572.33, -81.22) * mm, "mid": v(574.98, -80.12) * mm, "end": v(576.08, -77.47) * mm});
            skArc(sketch, "E1018", {"start": v(576.08, -497.08) * mm, "mid": v(574.98, -494.43) * mm, "end": v(572.33, -493.33) * mm});
            skArc(sketch, "E1019", {"start": v(572.33, -493.33) * mm, "mid": v(569.68, -494.43) * mm, "end": v(568.58, -497.08) * mm});
            skArc(sketch, "E1020", {"start": v(568.58, -497.08) * mm, "mid": v(569.68, -499.73) * mm, "end": v(572.33, -500.83) * mm});
            skArc(sketch, "E1021", {"start": v(572.33, -500.83) * mm, "mid": v(574.98, -499.73) * mm, "end": v(576.08, -497.08) * mm});
            skArc(sketch, "E1022", {"start": v(576.08, -347.08) * mm, "mid": v(574.98, -344.43) * mm, "end": v(572.33, -343.33) * mm});
            skArc(sketch, "E1023", {"start": v(572.33, -343.33) * mm, "mid": v(569.68, -344.43) * mm, "end": v(568.58, -347.08) * mm});
            skArc(sketch, "E1024", {"start": v(568.58, -347.08) * mm, "mid": v(569.68, -349.73) * mm, "end": v(572.33, -350.83) * mm});
            skArc(sketch, "E1025", {"start": v(572.33, -350.83) * mm, "mid": v(574.98, -349.73) * mm, "end": v(576.08, -347.08) * mm});
            skArc(sketch, "E1026", {"start": v(576.08, -647.08) * mm, "mid": v(574.98, -644.43) * mm, "end": v(572.33, -643.33) * mm});
            skArc(sketch, "E1027", {"start": v(572.33, -643.33) * mm, "mid": v(569.68, -644.43) * mm, "end": v(568.58, -647.08) * mm});
            skArc(sketch, "E1028", {"start": v(568.58, -647.08) * mm, "mid": v(569.68, -649.73) * mm, "end": v(572.33, -650.83) * mm});
            skArc(sketch, "E1029", {"start": v(572.33, -650.83) * mm, "mid": v(574.98, -649.73) * mm, "end": v(576.08, -647.08) * mm});
            skArc(sketch, "E1030", {"start": v(576.08, -767.08) * mm, "mid": v(574.98, -764.43) * mm, "end": v(572.33, -763.33) * mm});
            skArc(sketch, "E1031", {"start": v(572.33, -763.33) * mm, "mid": v(569.68, -764.43) * mm, "end": v(568.58, -767.08) * mm});
            skArc(sketch, "E1032", {"start": v(568.58, -767.08) * mm, "mid": v(569.68, -769.73) * mm, "end": v(572.33, -770.83) * mm});
            skArc(sketch, "E1033", {"start": v(572.33, -770.83) * mm, "mid": v(574.98, -769.73) * mm, "end": v(576.08, -767.08) * mm});
            skArc(sketch, "E1034", {"start": v(576.08, -947.08) * mm, "mid": v(574.98, -944.43) * mm, "end": v(572.33, -943.33) * mm});
            skArc(sketch, "E1035", {"start": v(572.33, -943.33) * mm, "mid": v(569.68, -944.43) * mm, "end": v(568.58, -947.08) * mm});
            skArc(sketch, "E1036", {"start": v(568.58, -947.08) * mm, "mid": v(569.68, -949.73) * mm, "end": v(572.33, -950.83) * mm});
            skArc(sketch, "E1037", {"start": v(572.33, -950.83) * mm, "mid": v(574.98, -949.73) * mm, "end": v(576.08, -947.08) * mm});
            skArc(sketch, "E1038", {"start": v(576.08, -1067.26) * mm, "mid": v(574.98, -1064.6) * mm, "end": v(572.33, -1063.5) * mm});
            skArc(sketch, "E1039", {"start": v(572.33, -1063.5) * mm, "mid": v(569.68, -1064.6) * mm, "end": v(568.58, -1067.26) * mm});
            skArc(sketch, "E1040", {"start": v(568.58, -1067.26) * mm, "mid": v(569.68, -1069.9) * mm, "end": v(572.33, -1071) * mm});
            skArc(sketch, "E1041", {"start": v(572.33, -1071) * mm, "mid": v(574.98, -1069.9) * mm, "end": v(576.08, -1067.26) * mm});
            skArc(sketch, "E1042", {"start": v(576.08, -827.08) * mm, "mid": v(574.98, -824.43) * mm, "end": v(572.33, -823.33) * mm});
            skArc(sketch, "E1043", {"start": v(572.33, -823.33) * mm, "mid": v(569.68, -824.43) * mm, "end": v(568.58, -827.08) * mm});
            skArc(sketch, "E1044", {"start": v(568.58, -827.08) * mm, "mid": v(569.68, -829.73) * mm, "end": v(572.33, -830.83) * mm});
            skArc(sketch, "E1045", {"start": v(572.33, -830.83) * mm, "mid": v(574.98, -829.73) * mm, "end": v(576.08, -827.08) * mm});
            skArc(sketch, "E1046", {"start": v(-568.73, 1161.23) * mm, "mid": v(-569.83, 1163.88) * mm, "end": v(-572.48, 1164.98) * mm});
            skArc(sketch, "E1047", {"start": v(-572.48, 1164.98) * mm, "mid": v(-575.13, 1163.88) * mm, "end": v(-576.23, 1161.23) * mm});
            skArc(sketch, "E1048", {"start": v(-576.23, 1161.23) * mm, "mid": v(-575.13, 1158.58) * mm, "end": v(-572.48, 1157.48) * mm});
            skArc(sketch, "E1049", {"start": v(-572.48, 1157.48) * mm, "mid": v(-569.83, 1158.58) * mm, "end": v(-568.73, 1161.23) * mm});
            skArc(sketch, "E1050", {"start": v(-568.73, 924.6) * mm, "mid": v(-569.83, 927.26) * mm, "end": v(-572.48, 928.36) * mm});
            skArc(sketch, "E1051", {"start": v(-572.48, 928.36) * mm, "mid": v(-575.13, 927.26) * mm, "end": v(-576.23, 924.6) * mm});
            skArc(sketch, "E1052", {"start": v(-576.23, 924.6) * mm, "mid": v(-575.13, 921.96) * mm, "end": v(-572.48, 920.86) * mm});
            skArc(sketch, "E1053", {"start": v(-572.48, 920.86) * mm, "mid": v(-569.83, 921.96) * mm, "end": v(-568.73, 924.6) * mm});
            skArc(sketch, "E1054", {"start": v(-568.73, 854.1) * mm, "mid": v(-569.83, 856.75) * mm, "end": v(-572.48, 857.85) * mm});
            skArc(sketch, "E1055", {"start": v(-572.48, 857.85) * mm, "mid": v(-575.13, 856.75) * mm, "end": v(-576.23, 854.1) * mm});
            skArc(sketch, "E1056", {"start": v(-576.23, 854.1) * mm, "mid": v(-575.13, 851.45) * mm, "end": v(-572.48, 850.35) * mm});
            skArc(sketch, "E1057", {"start": v(-572.48, 850.35) * mm, "mid": v(-569.83, 851.45) * mm, "end": v(-568.73, 854.1) * mm});
            skArc(sketch, "E1058", {"start": v(-568.73, 1041.06) * mm, "mid": v(-569.83, 1043.72) * mm, "end": v(-572.48, 1044.81) * mm});
            skArc(sketch, "E1059", {"start": v(-572.48, 1044.81) * mm, "mid": v(-575.13, 1043.72) * mm, "end": v(-576.23, 1041.06) * mm});
            skArc(sketch, "E1060", {"start": v(-576.23, 1041.06) * mm, "mid": v(-575.13, 1038.41) * mm, "end": v(-572.48, 1037.31) * mm});
            skArc(sketch, "E1061", {"start": v(-572.48, 1037.31) * mm, "mid": v(-569.83, 1038.41) * mm, "end": v(-568.73, 1041.06) * mm});
            skArc(sketch, "E1062", {"start": v(-568.73, 589.45) * mm, "mid": v(-569.83, 592.1) * mm, "end": v(-572.48, 593.2) * mm});
            skArc(sketch, "E1063", {"start": v(-572.48, 593.2) * mm, "mid": v(-575.13, 592.1) * mm, "end": v(-576.23, 589.45) * mm});
            skArc(sketch, "E1064", {"start": v(-576.23, 589.45) * mm, "mid": v(-575.13, 586.8) * mm, "end": v(-572.48, 585.7) * mm});
            skArc(sketch, "E1065", {"start": v(-572.48, 585.7) * mm, "mid": v(-569.83, 586.8) * mm, "end": v(-568.73, 589.45) * mm});
            skArc(sketch, "E1066", {"start": v(-568.73, 729.1) * mm, "mid": v(-569.83, 731.75) * mm, "end": v(-572.48, 732.85) * mm});
            skArc(sketch, "E1067", {"start": v(-572.48, 732.85) * mm, "mid": v(-575.13, 731.75) * mm, "end": v(-576.23, 729.1) * mm});
            skArc(sketch, "E1068", {"start": v(-576.23, 729.1) * mm, "mid": v(-575.13, 726.45) * mm, "end": v(-572.48, 725.35) * mm});
            skArc(sketch, "E1069", {"start": v(-572.48, 725.35) * mm, "mid": v(-569.83, 726.45) * mm, "end": v(-568.73, 729.1) * mm});
            skArc(sketch, "E1070", {"start": v(-568.73, 439.45) * mm, "mid": v(-569.83, 442.1) * mm, "end": v(-572.48, 443.2) * mm});
            skArc(sketch, "E1071", {"start": v(-572.48, 443.2) * mm, "mid": v(-575.13, 442.1) * mm, "end": v(-576.23, 439.45) * mm});
            skArc(sketch, "E1072", {"start": v(-576.23, 439.45) * mm, "mid": v(-575.13, 436.8) * mm, "end": v(-572.48, 435.7) * mm});
            skArc(sketch, "E1073", {"start": v(-572.48, 435.7) * mm, "mid": v(-569.83, 436.8) * mm, "end": v(-568.73, 439.45) * mm});
            skArc(sketch, "E1074", {"start": v(-568.73, 289.45) * mm, "mid": v(-569.83, 292.1) * mm, "end": v(-572.48, 293.2) * mm});
            skArc(sketch, "E1075", {"start": v(-572.48, 293.2) * mm, "mid": v(-575.13, 292.1) * mm, "end": v(-576.23, 289.45) * mm});
            skArc(sketch, "E1076", {"start": v(-576.23, 289.45) * mm, "mid": v(-575.13, 286.8) * mm, "end": v(-572.48, 285.7) * mm});
            skArc(sketch, "E1077", {"start": v(-572.48, 285.7) * mm, "mid": v(-569.83, 286.8) * mm, "end": v(-568.73, 289.45) * mm});
            skArc(sketch, "E1078", {"start": v(-568.73, 167.99) * mm, "mid": v(-569.83, 170.64) * mm, "end": v(-572.48, 171.74) * mm});
            skArc(sketch, "E1079", {"start": v(-572.48, 171.74) * mm, "mid": v(-575.13, 170.64) * mm, "end": v(-576.23, 167.99) * mm});
            skArc(sketch, "E1080", {"start": v(-576.23, 167.99) * mm, "mid": v(-575.13, 165.34) * mm, "end": v(-572.48, 164.24) * mm});
            skArc(sketch, "E1081", {"start": v(-572.48, 164.24) * mm, "mid": v(-569.83, 165.34) * mm, "end": v(-568.73, 167.99) * mm});
            skArc(sketch, "E1082", {"start": v(-568.73, 46.3) * mm, "mid": v(-569.83, 48.95) * mm, "end": v(-572.48, 50.05) * mm});
            skArc(sketch, "E1083", {"start": v(-572.48, 50.05) * mm, "mid": v(-575.13, 48.95) * mm, "end": v(-576.23, 46.3) * mm});
            skArc(sketch, "E1084", {"start": v(-576.23, 46.3) * mm, "mid": v(-575.13, 43.65) * mm, "end": v(-572.48, 42.55) * mm});
            skArc(sketch, "E1085", {"start": v(-572.48, 42.55) * mm, "mid": v(-569.83, 43.65) * mm, "end": v(-568.73, 46.3) * mm});
            skArc(sketch, "E1086", {"start": v(-568.73, -197.02) * mm, "mid": v(-569.83, -194.36) * mm, "end": v(-572.48, -193.27) * mm});
            skArc(sketch, "E1087", {"start": v(-572.48, -193.27) * mm, "mid": v(-575.13, -194.36) * mm, "end": v(-576.23, -197.02) * mm});
            skArc(sketch, "E1088", {"start": v(-576.23, -197.02) * mm, "mid": v(-575.13, -199.67) * mm, "end": v(-572.48, -200.77) * mm});
            skArc(sketch, "E1089", {"start": v(-572.48, -200.77) * mm, "mid": v(-569.83, -199.67) * mm, "end": v(-568.73, -197.02) * mm});
            skArc(sketch, "E1090", {"start": v(-568.73, -77.47) * mm, "mid": v(-569.83, -74.82) * mm, "end": v(-572.48, -73.72) * mm});
            skArc(sketch, "E1091", {"start": v(-572.48, -73.72) * mm, "mid": v(-575.13, -74.82) * mm, "end": v(-576.23, -77.47) * mm});
            skArc(sketch, "E1092", {"start": v(-576.23, -77.47) * mm, "mid": v(-575.13, -80.12) * mm, "end": v(-572.48, -81.22) * mm});
            skArc(sketch, "E1093", {"start": v(-572.48, -81.22) * mm, "mid": v(-569.83, -80.12) * mm, "end": v(-568.73, -77.47) * mm});
            skArc(sketch, "E1094", {"start": v(-568.73, -497.08) * mm, "mid": v(-569.83, -494.43) * mm, "end": v(-572.48, -493.33) * mm});
            skArc(sketch, "E1095", {"start": v(-572.48, -493.33) * mm, "mid": v(-575.13, -494.43) * mm, "end": v(-576.23, -497.08) * mm});
            skArc(sketch, "E1096", {"start": v(-576.23, -497.08) * mm, "mid": v(-575.13, -499.73) * mm, "end": v(-572.48, -500.83) * mm});
            skArc(sketch, "E1097", {"start": v(-572.48, -500.83) * mm, "mid": v(-569.83, -499.73) * mm, "end": v(-568.73, -497.08) * mm});
            skArc(sketch, "E1098", {"start": v(-568.73, -347.08) * mm, "mid": v(-569.83, -344.43) * mm, "end": v(-572.48, -343.33) * mm});
            skArc(sketch, "E1099", {"start": v(-572.48, -343.33) * mm, "mid": v(-575.13, -344.43) * mm, "end": v(-576.23, -347.08) * mm});
            skArc(sketch, "E1100", {"start": v(-576.23, -347.08) * mm, "mid": v(-575.13, -349.73) * mm, "end": v(-572.48, -350.83) * mm});
            skArc(sketch, "E1101", {"start": v(-572.48, -350.83) * mm, "mid": v(-569.83, -349.73) * mm, "end": v(-568.73, -347.08) * mm});
            skArc(sketch, "E1102", {"start": v(-568.73, -647.08) * mm, "mid": v(-569.83, -644.43) * mm, "end": v(-572.48, -643.33) * mm});
            skArc(sketch, "E1103", {"start": v(-572.48, -643.33) * mm, "mid": v(-575.13, -644.43) * mm, "end": v(-576.23, -647.08) * mm});
            skArc(sketch, "E1104", {"start": v(-576.23, -647.08) * mm, "mid": v(-575.13, -649.73) * mm, "end": v(-572.48, -650.83) * mm});
            skArc(sketch, "E1105", {"start": v(-572.48, -650.83) * mm, "mid": v(-569.83, -649.73) * mm, "end": v(-568.73, -647.08) * mm});
            skArc(sketch, "E1106", {"start": v(-568.73, -767.08) * mm, "mid": v(-569.83, -764.43) * mm, "end": v(-572.48, -763.33) * mm});
            skArc(sketch, "E1107", {"start": v(-572.48, -763.33) * mm, "mid": v(-575.13, -764.43) * mm, "end": v(-576.23, -767.08) * mm});
            skArc(sketch, "E1108", {"start": v(-576.23, -767.08) * mm, "mid": v(-575.13, -769.73) * mm, "end": v(-572.48, -770.83) * mm});
            skArc(sketch, "E1109", {"start": v(-572.48, -770.83) * mm, "mid": v(-569.83, -769.73) * mm, "end": v(-568.73, -767.08) * mm});
            skArc(sketch, "E1110", {"start": v(-568.73, -947.08) * mm, "mid": v(-569.83, -944.43) * mm, "end": v(-572.48, -943.33) * mm});
            skArc(sketch, "E1111", {"start": v(-572.48, -943.33) * mm, "mid": v(-575.13, -944.43) * mm, "end": v(-576.23, -947.08) * mm});
            skArc(sketch, "E1112", {"start": v(-576.23, -947.08) * mm, "mid": v(-575.13, -949.73) * mm, "end": v(-572.48, -950.83) * mm});
            skArc(sketch, "E1113", {"start": v(-572.48, -950.83) * mm, "mid": v(-569.83, -949.73) * mm, "end": v(-568.73, -947.08) * mm});
            skArc(sketch, "E1114", {"start": v(-568.73, -1067.26) * mm, "mid": v(-569.83, -1064.6) * mm, "end": v(-572.48, -1063.5) * mm});
            skArc(sketch, "E1115", {"start": v(-572.48, -1063.5) * mm, "mid": v(-575.13, -1064.6) * mm, "end": v(-576.23, -1067.26) * mm});
            skArc(sketch, "E1116", {"start": v(-576.23, -1067.26) * mm, "mid": v(-575.13, -1069.9) * mm, "end": v(-572.48, -1071) * mm});
            skArc(sketch, "E1117", {"start": v(-572.48, -1071) * mm, "mid": v(-569.83, -1069.9) * mm, "end": v(-568.73, -1067.26) * mm});
            skArc(sketch, "E1118", {"start": v(-568.73, -827.08) * mm, "mid": v(-569.83, -824.43) * mm, "end": v(-572.48, -823.33) * mm});
            skArc(sketch, "E1119", {"start": v(-572.48, -823.33) * mm, "mid": v(-575.13, -824.43) * mm, "end": v(-576.23, -827.08) * mm});
            skArc(sketch, "E1120", {"start": v(-576.23, -827.08) * mm, "mid": v(-575.13, -829.73) * mm, "end": v(-572.48, -830.83) * mm});
            skArc(sketch, "E1121", {"start": v(-572.48, -830.83) * mm, "mid": v(-569.83, -829.73) * mm, "end": v(-568.73, -827.08) * mm});
            skArc(sketch, "E1122", {"start": v(-2.75, -956.94) * mm, "mid": v(-5.4, -958.04) * mm, "end": v(-6.5, -960.69) * mm});
            skArc(sketch, "E1123", {"start": v(-6.5, -960.69) * mm, "mid": v(-5.4, -963.34) * mm, "end": v(-2.75, -964.44) * mm});
            skArc(sketch, "E1124", {"start": v(-2.75, -964.44) * mm, "mid": v(-0.1, -963.34) * mm, "end": v(1, -960.69) * mm});
            skArc(sketch, "E1125", {"start": v(1, -960.69) * mm, "mid": v(-0.1, -958.04) * mm, "end": v(-2.75, -956.94) * mm});
            skArc(sketch, "E1126", {"start": v(-12.14, -337.28) * mm, "mid": v(-14.8, -338.38) * mm, "end": v(-15.9, -341.03) * mm});
            skArc(sketch, "E1127", {"start": v(-15.9, -341.03) * mm, "mid": v(-14.8, -343.69) * mm, "end": v(-12.14, -344.78) * mm});
            skArc(sketch, "E1128", {"start": v(-12.14, -344.78) * mm, "mid": v(-9.5, -343.69) * mm, "end": v(-8.4, -341.03) * mm});
            skArc(sketch, "E1129", {"start": v(-8.4, -341.03) * mm, "mid": v(-9.5, -338.38) * mm, "end": v(-12.14, -337.28) * mm});
            skArc(sketch, "E1130", {"start": v(-2.75, 1108.58) * mm, "mid": v(-5.4, 1107.48) * mm, "end": v(-6.5, 1104.83) * mm});
            skArc(sketch, "E1131", {"start": v(-6.5, 1104.83) * mm, "mid": v(-5.4, 1102.17) * mm, "end": v(-2.75, 1101.08) * mm});
            skArc(sketch, "E1132", {"start": v(-2.75, 1101.08) * mm, "mid": v(-0.1, 1102.17) * mm, "end": v(1, 1104.83) * mm});
            skArc(sketch, "E1133", {"start": v(1, 1104.83) * mm, "mid": v(-0.1, 1107.48) * mm, "end": v(-2.75, 1108.58) * mm});
            skArc(sketch, "E1134", {"start": v(1.94, 686.08) * mm, "mid": v(-0.71, 684.99) * mm, "end": v(-1.8, 682.33) * mm});
            skArc(sketch, "E1135", {"start": v(-1.8, 682.33) * mm, "mid": v(-0.71, 679.68) * mm, "end": v(1.94, 678.58) * mm});
            skArc(sketch, "E1136", {"start": v(1.94, 678.58) * mm, "mid": v(4.6, 679.68) * mm, "end": v(5.7, 682.33) * mm});
            skArc(sketch, "E1137", {"start": v(5.7, 682.33) * mm, "mid": v(4.6, 684.99) * mm, "end": v(1.94, 686.08) * mm});
            skArc(sketch, "E1138", {"start": v(-2.75, 193.18) * mm, "mid": v(-5.4, 192.08) * mm, "end": v(-6.5, 189.43) * mm});
            skArc(sketch, "E1139", {"start": v(-6.5, 189.43) * mm, "mid": v(-5.4, 186.78) * mm, "end": v(-2.75, 185.68) * mm});
            skArc(sketch, "E1140", {"start": v(-2.75, 185.68) * mm, "mid": v(-0.1, 186.78) * mm, "end": v(1, 189.43) * mm});
            skArc(sketch, "E1141", {"start": v(1, 189.43) * mm, "mid": v(-0.1, 192.08) * mm, "end": v(-2.75, 193.18) * mm});
            skArc(sketch, "E1142", {"start": v(-522.9, -1110.19) * mm, "mid": v(-525.55, -1111.29) * mm, "end": v(-526.65, -1113.94) * mm});
            skArc(sketch, "E1143", {"start": v(-526.65, -1113.94) * mm, "mid": v(-525.55, -1116.59) * mm, "end": v(-522.9, -1117.69) * mm});
            skArc(sketch, "E1144", {"start": v(-522.9, -1117.69) * mm, "mid": v(-520.25, -1116.59) * mm, "end": v(-519.15, -1113.94) * mm});
            skArc(sketch, "E1145", {"start": v(-519.15, -1113.94) * mm, "mid": v(-520.25, -1111.29) * mm, "end": v(-522.9, -1110.19) * mm});
            skArc(sketch, "E1146", {"start": v(-170.95, -1111.42) * mm, "mid": v(-173.6, -1112.52) * mm, "end": v(-174.7, -1115.17) * mm});
            skArc(sketch, "E1147", {"start": v(-174.7, -1115.17) * mm, "mid": v(-173.6, -1117.82) * mm, "end": v(-170.95, -1118.92) * mm});
            skArc(sketch, "E1148", {"start": v(-170.95, -1118.92) * mm, "mid": v(-168.3, -1117.82) * mm, "end": v(-167.2, -1115.17) * mm});
            skArc(sketch, "E1149", {"start": v(-167.2, -1115.17) * mm, "mid": v(-168.3, -1112.52) * mm, "end": v(-170.95, -1111.42) * mm});
            skArc(sketch, "E1150", {"start": v(173.62, -1108.96) * mm, "mid": v(170.97, -1110.06) * mm, "end": v(169.87, -1112.7) * mm});
            skArc(sketch, "E1151", {"start": v(169.87, -1112.7) * mm, "mid": v(170.97, -1115.36) * mm, "end": v(173.62, -1116.46) * mm});
            skArc(sketch, "E1152", {"start": v(173.62, -1116.46) * mm, "mid": v(176.27, -1115.36) * mm, "end": v(177.37, -1112.7) * mm});
            skArc(sketch, "E1153", {"start": v(177.37, -1112.7) * mm, "mid": v(176.27, -1110.06) * mm, "end": v(173.62, -1108.96) * mm});
            skArc(sketch, "E1154", {"start": v(520.65, -1110.19) * mm, "mid": v(518, -1111.29) * mm, "end": v(516.9, -1113.94) * mm});
            skArc(sketch, "E1155", {"start": v(516.9, -1113.94) * mm, "mid": v(518, -1116.59) * mm, "end": v(520.65, -1117.69) * mm});
            skArc(sketch, "E1156", {"start": v(520.65, -1117.69) * mm, "mid": v(523.3, -1116.59) * mm, "end": v(524.4, -1113.94) * mm});
            skArc(sketch, "E1157", {"start": v(524.4, -1113.94) * mm, "mid": v(523.3, -1111.29) * mm, "end": v(520.65, -1110.19) * mm});
            skSolve(sketch);
        }
        {
            var Q0;
            Q0=makeQuery(id+"F0.imprint","IMPRINT",FACE,{"disambiguationData":[TD([[makeQuery(id+"F0.imprint","IMPRINT",EDGE,{"derivedFrom":sQuery(id+"F0.wireOp",EDGE,"E0")}),1.0]])]});
            var Q1;
            {var subQ0=sQuery(id+"F0.wireOp",EDGE,"E821");Q1=makeQuery(id+"F0.imprint","IMPRINT",FACE,{"disambiguationData":[TD([[makeQuery(id+"F0.imprint","IMPRINT",EDGE,{"derivedFrom":subQ0}),-1.0]])]});}
            var Q2;
            Q2=makeQuery(id+"F0.imprint","IMPRINT",FACE,{"disambiguationData":[TD([[makeQuery(id+"F0.imprint","IMPRINT",EDGE,{"derivedFrom":sQuery(id+"F0.wireOp",EDGE,"E564")}),-1.0]])]});
            var Q3;
            Q3=makeQuery(id+"F0.imprint","IMPRINT",FACE,{"disambiguationData":[TD([[makeQuery(id+"F0.imprint","IMPRINT",EDGE,{"derivedFrom":sQuery(id+"F0.wireOp",EDGE,"E308")}),-1.0]])]});
            extrude(context, id + "F1", {"entities" : qUnion([Q0, Q1, Q2, Q3]), "depth" : 18 * mm});
        }
    });
